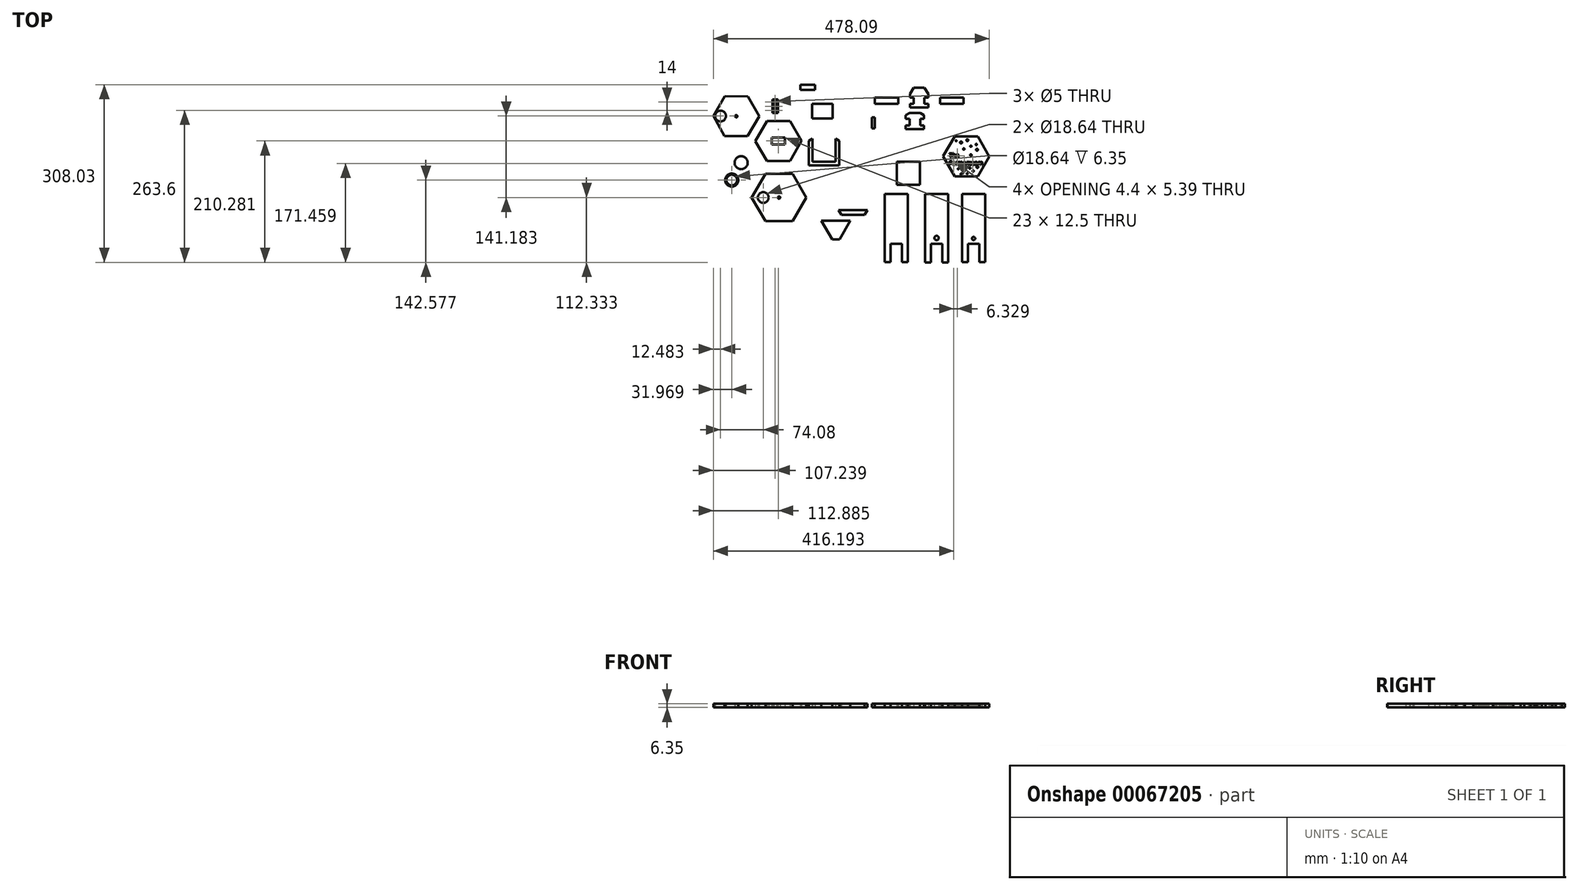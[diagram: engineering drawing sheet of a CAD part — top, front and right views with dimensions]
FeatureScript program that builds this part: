
annotation { "Feature Type Name" : "Feature", "Feature Type Description" : "" }
export const myFeature = defineFeature(function(context is Context, id is Id, definition is map)
    precondition{}
    {
        {
            var Q0;
            Q0=qCreatedBy(makeId("Top.planeOp"),FACE);
            var sketch = newSketch(context, id + "F0", { "sketchPlane" : qUnion([Q0])});
            skLineSegment(sketch, "E0.bottom", {"start": v(13.19, 75.62) * mm, "end": v(53.19, 75.62) * mm});
            skLineSegment(sketch, "E0.left", {"start": v(13.19, 75.62) * mm, "end": v(13.19, -42.73) * mm});
            skLineSegment(sketch, "E0.right", {"start": v(53.19, 75.62) * mm, "end": v(53.19, -42.73) * mm});
            skLineSegment(sketch, "E1.top", {"start": v(23.19, -10.73) * mm, "end": v(43.19, -10.73) * mm});
            skLineSegment(sketch, "E1.left", {"start": v(23.19, -42.73) * mm, "end": v(23.19, -10.73) * mm});
            skLineSegment(sketch, "E1.right", {"start": v(43.19, -42.73) * mm, "end": v(43.19, -10.73) * mm});
            skLineSegment(sketch, "E2", {"start": v(23.19, -42.73) * mm, "end": v(13.19, -42.73) * mm});
            skLineSegment(sketch, "E3", {"start": v(53.19, -42.73) * mm, "end": v(43.19, -42.73) * mm});
            skCircle(sketch, "E4.cCircle", {"center": v(-113.78, 34.64) * mm, "radius": 40 * mm, "construction": true});
            skLineSegment(sketch, "E4.0", {"start": v(-73.79, 34.86) * mm, "end": v(-93.6, 0.11) * mm});
            skLineSegment(sketch, "E4.1", {"start": v(-93.6, 0.11) * mm, "end": v(-133.6, -0.1) * mm});
            skLineSegment(sketch, "E4.2", {"start": v(-133.6, -0.1) * mm, "end": v(-153.78, 34.42) * mm});
            skLineSegment(sketch, "E4.3", {"start": v(-153.78, 34.42) * mm, "end": v(-133.97, 69.17) * mm});
            skLineSegment(sketch, "E4.4", {"start": v(-133.97, 69.17) * mm, "end": v(-93.98, 69.4) * mm});
            skLineSegment(sketch, "E4.5", {"start": v(-93.98, 69.4) * mm, "end": v(-73.79, 34.86) * mm});
            skCircle(sketch, "E5.cCircle", {"center": v(-112.79, -63.3) * mm, "radius": 47.33 * mm, "construction": true});
            skLineSegment(sketch, "E5.0", {"start": v(-89.12, -104.3) * mm, "end": v(-136.45, -104.3) * mm});
            skLineSegment(sketch, "E5.1", {"start": v(-136.45, -104.3) * mm, "end": v(-160.12, -63.3) * mm});
            skLineSegment(sketch, "E5.2", {"start": v(-160.12, -63.3) * mm, "end": v(-136.45, -22.32) * mm});
            skLineSegment(sketch, "E5.3", {"start": v(-136.45, -22.32) * mm, "end": v(-89.12, -22.32) * mm});
            skLineSegment(sketch, "E5.4", {"start": v(-89.12, -22.32) * mm, "end": v(-65.46, -63.3) * mm});
            skLineSegment(sketch, "E5.5", {"start": v(-65.46, -63.3) * mm, "end": v(-89.12, -104.3) * mm});
            skCircle(sketch, "E6", {"center": v(-112.79, -63.3) * mm, "radius": 2 * mm});
            skLineSegment(sketch, "E7", {"start": v(-112.79, -63.3) * mm, "end": v(-160.12, -63.3) * mm});
            skCircle(sketch, "E8", {"center": v(-140.1, -63.3) * mm, "radius": 9.32 * mm});
            skLineSegment(sketch, "E9", {"start": v(-130.79, -63.3) * mm, "end": v(-114.79, -63.3) * mm});
            skCircle(sketch, "E10", {"center": v(-178.44, -3) * mm, "radius": 11.32 * mm});
            skCircle(sketch, "E11.cCircle", {"center": v(211.42, 8.02) * mm, "radius": 40 * mm, "construction": true});
            skLineSegment(sketch, "E11.0", {"start": v(231.66, 42.52) * mm, "end": v(251.42, 7.74) * mm});
            skLineSegment(sketch, "E11.1", {"start": v(251.42, 7.74) * mm, "end": v(231.17, -26.76) * mm});
            skLineSegment(sketch, "E11.2", {"start": v(231.17, -26.76) * mm, "end": v(191.17, -26.48) * mm});
            skLineSegment(sketch, "E11.3", {"start": v(191.17, -26.48) * mm, "end": v(171.42, 8.3) * mm});
            skLineSegment(sketch, "E11.4", {"start": v(171.42, 8.3) * mm, "end": v(191.66, 42.8) * mm});
            skLineSegment(sketch, "E11.5", {"start": v(191.66, 42.8) * mm, "end": v(231.66, 42.52) * mm});
            skText(sketch, "E12", { "text": "The \nFermenteam", "fontName": "OpenSans-Regular.ttf"});
            skLineSegment(sketch, "E13.0", {"start": v(-8.24, -136.08) * mm, "end": v(-20.94, -136.08) * mm});
            skLineSegment(sketch, "E14", {"start": v(-39.59, -103.77) * mm, "end": v(10.41, -103.77) * mm});
            skLineSegment(sketch, "E15", {"start": v(-20.94, -136.08) * mm, "end": v(-39.59, -103.77) * mm});
            skLineSegment(sketch, "E16", {"start": v(-8.24, -136.08) * mm, "end": v(10.41, -103.77) * mm});
            skLineSegment(sketch, "E17", {"start": v(-9.58, -84.74) * mm, "end": v(40.42, -84.74) * mm});
            skLineSegment(sketch, "E18.0", {"start": v(35.42, -93.4) * mm, "end": v(-4.58, -93.4) * mm});
            skLineSegment(sketch, "E19", {"start": v(35.42, -93.4) * mm, "end": v(40.42, -84.74) * mm});
            skLineSegment(sketch, "E20", {"start": v(-4.58, -93.4) * mm, "end": v(-9.58, -84.74) * mm});
            skCircle(sketch, "E21", {"center": v(193.92, 34.98) * mm, "radius": 0.93 * mm});
            skCircle(sketch, "E22", {"center": v(202.28, 32.08) * mm, "radius": 1.74 * mm});
            skCircle(sketch, "E23.cCircle", {"center": v(-186.87, 77.62) * mm, "radius": 39.8 * mm, "construction": true});
            skLineSegment(sketch, "E23.0", {"start": v(-167.3, 42.96) * mm, "end": v(-207.1, 43.34) * mm});
            skLineSegment(sketch, "E23.1", {"start": v(-207.1, 43.34) * mm, "end": v(-226.67, 78) * mm});
            skLineSegment(sketch, "E23.2", {"start": v(-226.67, 78) * mm, "end": v(-206.44, 112.27) * mm});
            skLineSegment(sketch, "E23.3", {"start": v(-206.44, 112.27) * mm, "end": v(-166.64, 111.9) * mm});
            skLineSegment(sketch, "E23.4", {"start": v(-166.64, 111.9) * mm, "end": v(-147.07, 77.24) * mm});
            skLineSegment(sketch, "E23.5", {"start": v(-147.07, 77.24) * mm, "end": v(-167.3, 42.96) * mm});
            skCircle(sketch, "E24", {"center": v(213.2, 36.14) * mm, "radius": 1.66 * mm});
            skCircle(sketch, "E25", {"center": v(219.36, 25.57) * mm, "radius": 1.1 * mm});
            skCircle(sketch, "E26", {"center": v(207.04, 20.7) * mm, "radius": 1.3 * mm});
            skCircle(sketch, "E27", {"center": v(228.65, 28.6) * mm, "radius": 1.16 * mm});
            skCircle(sketch, "E28", {"center": v(230.04, 19.53) * mm, "radius": 1.66 * mm});
            skCircle(sketch, "E29", {"center": v(208.32, -15.2) * mm, "radius": 0.84 * mm});
            skCircle(sketch, "E30", {"center": v(223.38, -17.38) * mm, "radius": 1.2 * mm});
            skCircle(sketch, "E31", {"center": v(217.7, -12.44) * mm, "radius": 1.12 * mm});
            skCircle(sketch, "E32", {"center": v(197.6, -13.49) * mm, "radius": 0.82 * mm});
            skCircle(sketch, "E33", {"center": v(202.55, -22.64) * mm, "radius": 1.14 * mm});
            skCircle(sketch, "E34", {"center": v(212.88, -22.01) * mm, "radius": 0.77 * mm});
            skCircle(sketch, "E35", {"center": v(230.65, -10.5) * mm, "radius": 1.52 * mm});
            skCircle(sketch, "E36", {"center": v(219.28, 10.3) * mm, "radius": 1.41 * mm});
            skLineSegment(sketch, "E37.bottom", {"start": v(120.35, 127.23) * mm, "end": v(138.82, 127.23) * mm});
            skLineSegment(sketch, "E37.top", {"start": v(111.39, 92.46) * mm, "end": v(147.78, 92.46) * mm});
            skLineSegment(sketch, "E38", {"start": v(129.58, 92.46) * mm, "end": v(129.58, 110.79) * mm, "construction": true});
            skLineSegment(sketch, "E39.bottom", {"start": v(145.42, 92.46) * mm, "end": v(147.78, 92.46) * mm});
            skLineSegment(sketch, "E39.top", {"start": v(138.82, 98.81) * mm, "end": v(145.42, 98.81) * mm});
            skLineSegment(sketch, "E39.right", {"start": v(145.42, 92.46) * mm, "end": v(145.42, 98.81) * mm});
            skLineSegment(sketch, "E40.bottom", {"start": v(165.76, 98.81) * mm, "end": v(206.4, 98.81) * mm});
            skLineSegment(sketch, "E40.top", {"start": v(165.76, 109.97) * mm, "end": v(206.4, 109.97) * mm});
            skLineSegment(sketch, "E40.left", {"start": v(165.76, 98.81) * mm, "end": v(165.76, 109.97) * mm});
            skLineSegment(sketch, "E40.right", {"start": v(206.4, 98.81) * mm, "end": v(206.4, 109.97) * mm});
            skLineSegment(sketch, "E41.top", {"start": v(138.82, 109.97) * mm, "end": v(145.42, 109.97) * mm});
            skLineSegment(sketch, "E41.right", {"start": v(145.42, 116.46) * mm, "end": v(145.42, 109.97) * mm});
            skLineSegment(sketch, "E42", {"start": v(145.42, 116.46) * mm, "end": v(138.82, 127.23) * mm});
            skLineSegment(sketch, "E43", {"start": v(138.82, 109.97) * mm, "end": v(138.82, 98.81) * mm});
            skLineSegment(sketch, "E44", {"start": v(145.42, 109.97) * mm, "end": v(165.76, 109.97) * mm, "construction": true});
            skLineSegment(sketch, "E45", {"start": v(145.42, 98.81) * mm, "end": v(165.76, 98.81) * mm, "construction": true});
            skLineSegment(sketch, "E46", {"start": v(138.82, 127.23) * mm, "end": v(138.82, 109.97) * mm, "construction": true});
            skLineSegment(sketch, "E47.MirrorCS", {"start": v(93.4, 98.81) * mm, "end": v(93.4, 109.97) * mm});
            skLineSegment(sketch, "E48.MirrorCS", {"start": v(113.75, 109.97) * mm, "end": v(93.4, 109.97) * mm, "construction": true});
            skLineSegment(sketch, "E49.MirrorCS", {"start": v(93.4, 109.97) * mm, "end": v(52.77, 109.97) * mm});
            skLineSegment(sketch, "E50.MirrorCS", {"start": v(120.35, 109.97) * mm, "end": v(120.35, 98.81) * mm});
            skLineSegment(sketch, "E51.MirrorCS", {"start": v(93.4, 98.81) * mm, "end": v(52.77, 98.81) * mm});
            skLineSegment(sketch, "E52.MirrorCS", {"start": v(113.75, 116.46) * mm, "end": v(120.35, 127.23) * mm});
            skLineSegment(sketch, "E53.MirrorCS", {"start": v(113.75, 92.46) * mm, "end": v(113.75, 98.81) * mm});
            skLineSegment(sketch, "E54.MirrorCS", {"start": v(113.75, 116.46) * mm, "end": v(113.75, 109.97) * mm});
            skLineSegment(sketch, "E55.MirrorCS", {"start": v(120.35, 98.81) * mm, "end": v(113.75, 98.81) * mm});
            skLineSegment(sketch, "E56.MirrorCS", {"start": v(120.35, 109.97) * mm, "end": v(113.75, 109.97) * mm});
            skLineSegment(sketch, "E57.MirrorCS", {"start": v(113.75, 92.46) * mm, "end": v(111.39, 92.46) * mm});
            skLineSegment(sketch, "E58.MirrorCS", {"start": v(120.35, 127.23) * mm, "end": v(120.35, 109.97) * mm, "construction": true});
            skLineSegment(sketch, "E59.MirrorCS", {"start": v(52.77, 98.81) * mm, "end": v(52.77, 109.97) * mm});
            skLineSegment(sketch, "E60.MirrorCS", {"start": v(113.75, 98.81) * mm, "end": v(93.4, 98.81) * mm, "construction": true});
            skCircle(sketch, "E61", {"center": v(-194.7, -33.06) * mm, "radius": 11.32 * mm});
            skCircle(sketch, "E62", {"center": v(-194.7, -33.06) * mm, "radius": 9.32 * mm});
            skCircle(sketch, "E63", {"center": v(-194.7, -33.06) * mm, "radius": 12.32 * mm});
            skCircle(sketch, "E64", {"center": v(-186.87, 77.62) * mm, "radius": 2 * mm});
            skLineSegment(sketch, "E65", {"start": v(-226.67, 78) * mm, "end": v(-186.87, 77.62) * mm});
            skCircle(sketch, "E66", {"center": v(-214.19, 77.88) * mm, "radius": 9.32 * mm});
            skLineSegment(sketch, "E67", {"start": v(-188.87, 77.63) * mm, "end": v(-204.87, 77.79) * mm});
            skPoint(sketch, "E68.centerSnap0", {"position": v(33.19, 75.62) * mm});
            skLineSegment(sketch, "E69.bottom", {"start": v(113.25, 83.45) * mm, "end": v(131.72, 83.45) * mm});
            skLineSegment(sketch, "E70", {"start": v(131.72, 83.45) * mm, "end": v(131.72, 72.77) * mm, "construction": true});
            skLineSegment(sketch, "E71.top", {"start": v(131.72, 72.77) * mm, "end": v(138.32, 72.77) * mm});
            skLineSegment(sketch, "E72.MirrorCS", {"start": v(113.25, 72.77) * mm, "end": v(106.65, 72.77) * mm});
            skLineSegment(sketch, "E69.top", {"start": v(116.48, 55.26) * mm, "end": v(128.49, 55.26) * mm});
            skLineSegment(sketch, "E73.MirrorCS", {"start": v(113.25, 72.77) * mm, "end": v(113.25, 61.61) * mm});
            skLineSegment(sketch, "E74.top", {"start": v(131.72, 61.61) * mm, "end": v(138.32, 61.61) * mm});
            skLineSegment(sketch, "E75", {"start": v(122.48, 55.26) * mm, "end": v(122.48, 72.64) * mm, "construction": true});
            skLineSegment(sketch, "E76.MirrorCS", {"start": v(106.65, 72.77) * mm, "end": v(74.12, 72.77) * mm, "construction": true});
            skLineSegment(sketch, "E77.MirrorCS", {"start": v(116.48, 55.26) * mm, "end": v(106.65, 55.26) * mm});
            skLineSegment(sketch, "E71.right", {"start": v(138.32, 79.26) * mm, "end": v(138.32, 72.77) * mm});
            skLineSegment(sketch, "E78.MirrorCS", {"start": v(113.25, 83.45) * mm, "end": v(113.25, 72.77) * mm, "construction": true});
            skLineSegment(sketch, "E74.right", {"start": v(138.32, 55.26) * mm, "end": v(138.32, 61.61) * mm});
            skLineSegment(sketch, "E79", {"start": v(138.32, 79.26) * mm, "end": v(131.72, 83.45) * mm});
            skLineSegment(sketch, "E80.MirrorCS", {"start": v(106.65, 79.26) * mm, "end": v(113.25, 83.45) * mm});
            skLineSegment(sketch, "E81", {"start": v(131.72, 72.77) * mm, "end": v(131.72, 61.61) * mm});
            skLineSegment(sketch, "E74.bottom", {"start": v(128.49, 55.26) * mm, "end": v(138.32, 55.26) * mm});
            skLineSegment(sketch, "E82.MirrorCS", {"start": v(106.65, 55.26) * mm, "end": v(106.65, 61.61) * mm});
            skLineSegment(sketch, "E83", {"start": v(138.32, 72.77) * mm, "end": v(170.85, 72.77) * mm, "construction": true});
            skLineSegment(sketch, "E84.MirrorCS", {"start": v(106.65, 61.61) * mm, "end": v(86.31, 61.61) * mm, "construction": true});
            skLineSegment(sketch, "E85.MirrorCS", {"start": v(106.65, 79.26) * mm, "end": v(106.65, 72.77) * mm});
            skLineSegment(sketch, "E86", {"start": v(138.32, 61.61) * mm, "end": v(158.66, 61.61) * mm, "construction": true});
            skLineSegment(sketch, "E87.MirrorCS", {"start": v(113.25, 61.61) * mm, "end": v(106.65, 61.61) * mm});
            skLineSegment(sketch, "E88.rect.bottom", {"start": v(-102.28, 28.4) * mm, "end": v(-125.28, 28.4) * mm});
            skLineSegment(sketch, "E88.rect.top", {"start": v(-102.28, 40.9) * mm, "end": v(-125.28, 40.9) * mm});
            skLineSegment(sketch, "E88.rect.left", {"start": v(-102.28, 28.4) * mm, "end": v(-102.28, 40.9) * mm});
            skLineSegment(sketch, "E88.rect.right", {"start": v(-125.28, 28.4) * mm, "end": v(-125.28, 40.9) * mm});
            skLineSegment(sketch, "E89.bottom", {"start": v(-123.93, 106.46) * mm, "end": v(-114.93, 106.46) * mm});
            skLineSegment(sketch, "E89.top", {"start": v(-123.93, 83.46) * mm, "end": v(-114.93, 83.46) * mm});
            skLineSegment(sketch, "E89.left", {"start": v(-123.93, 106.46) * mm, "end": v(-123.93, 83.46) * mm});
            skLineSegment(sketch, "E89.right", {"start": v(-114.93, 106.46) * mm, "end": v(-114.93, 83.46) * mm});
            skLineSegment(sketch, "E90", {"start": v(-119.43, 106.46) * mm, "end": v(-119.43, 83.46) * mm});
            skCircle(sketch, "E91", {"center": v(-119.43, 101.96) * mm, "radius": 2.5 * mm});
            skCircle(sketch, "E92", {"center": v(-119.43, 94.96) * mm, "radius": 2.5 * mm});
            skCircle(sketch, "E93", {"center": v(-119.43, 87.96) * mm, "radius": 2.5 * mm});
            skLineSegment(sketch, "E94.bottom", {"start": v(131.41, -41.3) * mm, "end": v(91.41, -41.3) * mm});
            skLineSegment(sketch, "E94.top", {"start": v(131.41, -1.3) * mm, "end": v(91.41, -1.3) * mm});
            skLineSegment(sketch, "E94.left", {"start": v(131.41, -41.3) * mm, "end": v(131.41, -1.3) * mm});
            skLineSegment(sketch, "E94.right", {"start": v(91.41, -41.3) * mm, "end": v(91.41, -1.3) * mm});
            skPoint(sketch, "E94.middle", {"position": v(111.41, -21.3) * mm});
            skLineSegment(sketch, "E95.bottom", {"start": v(-50.7, 123.39) * mm, "end": v(-75.9, 123.39) * mm});
            skLineSegment(sketch, "E95.top", {"start": v(-50.7, 132.39) * mm, "end": v(-75.9, 132.39) * mm});
            skLineSegment(sketch, "E95.left", {"start": v(-50.7, 123.39) * mm, "end": v(-50.7, 132.39) * mm});
            skLineSegment(sketch, "E95.right", {"start": v(-75.9, 123.39) * mm, "end": v(-75.9, 132.39) * mm});
            skPoint(sketch, "E95.middle", {"position": v(-63.3, 127.89) * mm});
            skLineSegment(sketch, "E96.bottom", {"start": v(70.1, -56.84) * mm, "end": v(110.1, -56.84) * mm});
            skLineSegment(sketch, "E96.left", {"start": v(70.1, -56.84) * mm, "end": v(70.1, -175.19) * mm});
            skLineSegment(sketch, "E96.right", {"start": v(110.1, -56.84) * mm, "end": v(110.1, -175.19) * mm});
            skLineSegment(sketch, "E97.top", {"start": v(80.1, -143.19) * mm, "end": v(100.1, -143.19) * mm});
            skLineSegment(sketch, "E97.left", {"start": v(80.1, -175.19) * mm, "end": v(80.1, -143.19) * mm});
            skLineSegment(sketch, "E97.right", {"start": v(100.1, -175.19) * mm, "end": v(100.1, -143.19) * mm});
            skLineSegment(sketch, "E98", {"start": v(80.1, -175.19) * mm, "end": v(70.1, -175.19) * mm});
            skLineSegment(sketch, "E99", {"start": v(110.1, -175.19) * mm, "end": v(100.1, -175.19) * mm});
            skPoint(sketch, "E100.centerSnap0", {"position": v(90.1, -56.84) * mm});
            skLineSegment(sketch, "E101.bottom", {"start": v(139.95, -57.3) * mm, "end": v(179.95, -57.3) * mm});
            skLineSegment(sketch, "E101.left", {"start": v(139.95, -57.3) * mm, "end": v(139.95, -175.64) * mm});
            skLineSegment(sketch, "E101.right", {"start": v(179.95, -57.3) * mm, "end": v(179.95, -175.64) * mm});
            skLineSegment(sketch, "E102.top", {"start": v(149.95, -143.64) * mm, "end": v(169.95, -143.64) * mm});
            skLineSegment(sketch, "E102.left", {"start": v(149.95, -175.64) * mm, "end": v(149.95, -143.64) * mm});
            skLineSegment(sketch, "E102.right", {"start": v(169.95, -175.64) * mm, "end": v(169.95, -143.64) * mm});
            skLineSegment(sketch, "E103", {"start": v(149.95, -175.64) * mm, "end": v(139.95, -175.64) * mm});
            skLineSegment(sketch, "E104", {"start": v(179.95, -175.64) * mm, "end": v(169.95, -175.64) * mm});
            skPoint(sketch, "E105.centerSnap0", {"position": v(159.95, -57.3) * mm});
            skLineSegment(sketch, "E106", {"start": v(33.19, 75.62) * mm, "end": v(33.19, -10.73) * mm});
            skLineSegment(sketch, "E107", {"start": v(90.1, -56.84) * mm, "end": v(90.1, -143.19) * mm});
            skLineSegment(sketch, "E108", {"start": v(159.95, -57.3) * mm, "end": v(159.95, -143.64) * mm});
            skCircle(sketch, "E109", {"center": v(159.95, -133.48) * mm, "radius": 3.82 * mm});
            skLineSegment(sketch, "E110.bottom", {"start": v(-8.5, -7.82) * mm, "end": v(-61.2, -7.82) * mm});
            skLineSegment(sketch, "E110.top", {"start": v(-8.5, 44.88) * mm, "end": v(-61.2, 44.88) * mm});
            skLineSegment(sketch, "E110.left", {"start": v(-8.5, -7.82) * mm, "end": v(-8.5, 44.88) * mm});
            skLineSegment(sketch, "E110.right", {"start": v(-61.2, -7.82) * mm, "end": v(-61.2, 44.88) * mm});
            skPoint(sketch, "E110.middle", {"position": v(-34.84, 18.53) * mm});
            skLineSegment(sketch, "E111.bottom", {"start": v(-14.84, -1.47) * mm, "end": v(-54.84, -1.47) * mm});
            skLineSegment(sketch, "E111.top", {"start": v(-14.84, 38.53) * mm, "end": v(-54.84, 38.53) * mm});
            skLineSegment(sketch, "E111.left", {"start": v(-14.84, -1.47) * mm, "end": v(-14.84, 38.53) * mm});
            skLineSegment(sketch, "E111.right", {"start": v(-54.84, -1.47) * mm, "end": v(-54.84, 38.53) * mm});
            skLineSegment(sketch, "E112", {"start": v(-14.84, 38.53) * mm, "end": v(-8.5, 34.86) * mm});
            skLineSegment(sketch, "E113", {"start": v(-54.84, 38.53) * mm, "end": v(-61.2, 34.86) * mm});
            skLineSegment(sketch, "E114.bottom", {"start": v(204.1, -57.03) * mm, "end": v(244.1, -57.02) * mm});
            skLineSegment(sketch, "E114.left", {"start": v(204.1, -57.03) * mm, "end": v(204.1, -175.37) * mm});
            skLineSegment(sketch, "E114.right", {"start": v(244.1, -57.02) * mm, "end": v(244.1, -175.37) * mm});
            skLineSegment(sketch, "E115.top", {"start": v(214.1, -143.37) * mm, "end": v(234.1, -143.37) * mm});
            skLineSegment(sketch, "E115.left", {"start": v(214.1, -175.37) * mm, "end": v(214.1, -143.37) * mm});
            skLineSegment(sketch, "E115.right", {"start": v(234.1, -175.37) * mm, "end": v(234.1, -143.37) * mm});
            skLineSegment(sketch, "E116", {"start": v(214.1, -175.37) * mm, "end": v(204.1, -175.37) * mm});
            skLineSegment(sketch, "E117", {"start": v(244.1, -175.37) * mm, "end": v(234.1, -175.37) * mm});
            skPoint(sketch, "E118.centerSnap0", {"position": v(224.1, -57.03) * mm});
            skLineSegment(sketch, "E119", {"start": v(224.1, -57.03) * mm, "end": v(224.1, -143.37) * mm});
            skCircle(sketch, "E120", {"center": v(224.1, -134.27) * mm, "radius": 2.75 * mm});
            skLineSegment(sketch, "E121.bottom", {"start": v(116.41, 5.76) * mm, "end": v(106.41, 5.76) * mm});
            skLineSegment(sketch, "E121.top", {"start": v(116.41, -48.34) * mm, "end": v(106.41, -48.34) * mm});
            skLineSegment(sketch, "E121.left", {"start": v(116.41, 5.76) * mm, "end": v(116.41, -48.34) * mm});
            skLineSegment(sketch, "E121.right", {"start": v(106.41, 5.76) * mm, "end": v(106.41, -48.34) * mm});
            skLineSegment(sketch, "E122.bottom", {"start": v(-55.47, 98.98) * mm, "end": v(-19.77, 98.98) * mm});
            skLineSegment(sketch, "E122.top", {"start": v(-55.47, 73.78) * mm, "end": v(-19.77, 73.78) * mm});
            skLineSegment(sketch, "E122.left", {"start": v(-55.47, 98.98) * mm, "end": v(-55.47, 73.78) * mm});
            skLineSegment(sketch, "E122.right", {"start": v(-19.77, 98.98) * mm, "end": v(-19.77, 73.78) * mm});
            skLineSegment(sketch, "E123.bottom", {"start": v(53.19, 75.62) * mm, "end": v(48.19, 75.62) * mm});
            skLineSegment(sketch, "E123.top", {"start": v(53.19, 56.27) * mm, "end": v(48.19, 56.27) * mm});
            skLineSegment(sketch, "E123.left", {"start": v(53.19, 75.62) * mm, "end": v(53.19, 56.27) * mm});
            skLineSegment(sketch, "E123.right", {"start": v(48.19, 75.62) * mm, "end": v(48.19, 56.27) * mm});
            skLineSegment(sketch, "E124", {"start": v(48.19, 64.27) * mm, "end": v(53.19, 64.27) * mm});
            skCircle(sketch, "E125", {"center": v(33.19, 5.62) * mm, "radius": 2.6 * mm});
            const initialGuessF0  = {"E12": [0.18176, 0.00644, 1, 0, 0.007]};
            skSetInitialGuess(sketch, initialGuessF0);
            skSolve(sketch);
        }
        {
            var Q0;
            Q0=makeQuery(id+"F0.imprint","IMPRINT",FACE,{"disambiguationData":[TD([[makeQuery(id+"F0.imprint","IMPRINT",EDGE,{"derivedFrom":sQuery(id+"F0.wireOp",EDGE,"E4.0")}),-1.0]])]});
            var Q1;
            Q1=makeQuery(id+"F0.imprint","IMPRINT",FACE,{"disambiguationData":[TD([[makeQuery(id+"F0.imprint","IMPRINT",EDGE,{"derivedFrom":sQuery(id+"F0.wireOp",EDGE,"E10")}),1.0]])]});
            var Q2;
            Q2=makeQuery(id+"F0.imprint","IMPRINT",FACE,{"disambiguationData":[TD([[makeQuery(id+"F0.imprint","IMPRINT",EDGE,{"derivedFrom":sQuery(id+"F0.wireOp",EDGE,"E13.0")}),-1.0]])]});
            var Q3;
            Q3=makeQuery(id+"F0.imprint","IMPRINT",FACE,{"disambiguationData":[TD([[makeQuery(id+"F0.imprint","IMPRINT",EDGE,{"derivedFrom":sQuery(id+"F0.wireOp",EDGE,"E17")}),-1.0]])]});
            var Q4;
            Q4=makeQuery(id+"F0.imprint","IMPRINT",FACE,{"disambiguationData":[TD([[makeQuery(id+"F0.imprint","IMPRINT",EDGE,{"derivedFrom":sQuery(id+"F0.wireOp",EDGE,"E37.bottom")}),-1.0]])]});
            var Q5;
            Q5=makeQuery(id+"F0.imprint","IMPRINT",FACE,{"disambiguationData":[TD([[makeQuery(id+"F0.imprint","IMPRINT",EDGE,{"derivedFrom":sQuery(id+"F0.wireOp",EDGE,"E40.bottom")}),1.0]])]});
            var Q6;
            Q6=makeQuery(id+"F0.imprint","IMPRINT",FACE,{"disambiguationData":[TD([[makeQuery(id+"F0.imprint","IMPRINT",EDGE,{"derivedFrom":sQuery(id+"F0.wireOp",EDGE,"E47.MirrorCS")}),1.0]])]});
            var Q7;
            Q7=makeQuery(id+"F0.imprint","IMPRINT",FACE,{"disambiguationData":[TD([[makeQuery(id+"F0.imprint","IMPRINT",EDGE,{"derivedFrom":sQuery(id+"F0.wireOp",EDGE,"E0.bottom")}),-1.0]])]});
            var Q8;
            Q8=makeQuery(id+"F0.imprint","IMPRINT",FACE,{"disambiguationData":[TD([[makeQuery(id+"F0.imprint","IMPRINT",EDGE,{"derivedFrom":sQuery(id+"F0.wireOp",EDGE,"E61")}),1.0]])]});
            var Q9;
            Q9=makeQuery(id+"F0.imprint","IMPRINT",FACE,{"disambiguationData":[TD([[makeQuery(id+"F0.imprint","IMPRINT",EDGE,{"derivedFrom":sQuery(id+"F0.wireOp",EDGE,"E5.0")}),-1.0]])]});
            var Q10;
            Q10=makeQuery(id+"F0.imprint","IMPRINT",FACE,{"disambiguationData":[TD([[makeQuery(id+"F0.imprint","IMPRINT",EDGE,{"derivedFrom":sQuery(id+"F0.wireOp",EDGE,"E23.0")}),-1.0]])]});
            var Q11;
            Q11=makeQuery(id+"F0.imprint","IMPRINT",FACE,{"disambiguationData":[TD([[makeQuery(id+"F0.imprint","IMPRINT",EDGE,{"derivedFrom":sQuery(id+"F0.wireOp",EDGE,"E4.0")}),-1.0]])]});
            var Q12;
            Q12=makeQuery(id+"F0.imprint","IMPRINT",FACE,{"disambiguationData":[TD([[makeQuery(id+"F0.imprint","IMPRINT",EDGE,{"derivedFrom":sQuery(id+"F0.wireOp",EDGE,"E10")}),1.0]])]});
            var Q13;
            Q13=makeQuery(id+"F0.imprint","IMPRINT",FACE,{"disambiguationData":[TD([[makeQuery(id+"F0.imprint","IMPRINT",EDGE,{"derivedFrom":sQuery(id+"F0.wireOp",EDGE,"E13.0")}),-1.0]])]});
            var Q14;
            Q14=makeQuery(id+"F0.imprint","IMPRINT",FACE,{"disambiguationData":[TD([[makeQuery(id+"F0.imprint","IMPRINT",EDGE,{"derivedFrom":sQuery(id+"F0.wireOp",EDGE,"E17")}),-1.0]])]});
            var Q15;
            Q15=makeQuery(id+"F0.imprint","IMPRINT",FACE,{"disambiguationData":[TD([[makeQuery(id+"F0.imprint","IMPRINT",EDGE,{"derivedFrom":sQuery(id+"F0.wireOp",EDGE,"E37.bottom")}),-1.0]])]});
            var Q16;
            Q16=makeQuery(id+"F0.imprint","IMPRINT",FACE,{"disambiguationData":[TD([[makeQuery(id+"F0.imprint","IMPRINT",EDGE,{"derivedFrom":sQuery(id+"F0.wireOp",EDGE,"E40.bottom")}),1.0]])]});
            var Q17;
            Q17=makeQuery(id+"F0.imprint","IMPRINT",FACE,{"disambiguationData":[TD([[makeQuery(id+"F0.imprint","IMPRINT",EDGE,{"derivedFrom":sQuery(id+"F0.wireOp",EDGE,"E47.MirrorCS")}),1.0]])]});
            var Q18;
            Q18=makeQuery(id+"F0.imprint","IMPRINT",FACE,{"disambiguationData":[TD([[makeQuery(id+"F0.imprint","IMPRINT",EDGE,{"derivedFrom":sQuery(id+"F0.wireOp",EDGE,"E0.bottom")}),-1.0]])]});
            var Q19;
            Q19=makeQuery(id+"F0.imprint","IMPRINT",FACE,{"disambiguationData":[TD([[makeQuery(id+"F0.imprint","IMPRINT",EDGE,{"derivedFrom":sQuery(id+"F0.wireOp",EDGE,"E61")}),1.0]])]});
            var Q20;
            Q20=makeQuery(id+"F0.imprint","IMPRINT",FACE,{"disambiguationData":[TD([[makeQuery(id+"F0.imprint","IMPRINT",EDGE,{"derivedFrom":sQuery(id+"F0.wireOp",EDGE,"E5.0")}),-1.0]])]});
            var Q21;
            Q21=makeQuery(id+"F0.imprint","IMPRINT",FACE,{"disambiguationData":[TD([[makeQuery(id+"F0.imprint","IMPRINT",EDGE,{"derivedFrom":sQuery(id+"F0.wireOp",EDGE,"E23.0")}),-1.0]])]});
            var Q22;
            Q22=makeQuery(id+"F0.imprint","IMPRINT",FACE,{"disambiguationData":[TD([[makeQuery(id+"F0.imprint","IMPRINT",EDGE,{"derivedFrom":sQuery(id+"F0.wireOp",EDGE,"E61")}),1.0]])]});
            var Q23;
            Q23=makeQuery(id+"F0.imprint","IMPRINT",FACE,{"disambiguationData":[TD([[makeQuery(id+"F0.imprint","IMPRINT",EDGE,{"derivedFrom":sQuery(id+"F0.wireOp",EDGE,"E11.0")}),-1.0]])]});
            var Q24;
            {var subQ5=sQuery(id+"F0.wireOp",EDGE,"E89.left");Q24=makeQuery(id+"F0.imprint","IMPRINT",FACE,{"disambiguationData":[TD([[makeQuery(id+"F0.imprint","IMPRINT",EDGE,{"derivedFrom":subQ5}),1.0]])]});}
            var Q25;
            {var subQ5=sQuery(id+"F0.wireOp",EDGE,"E89.right");Q25=makeQuery(id+"F0.imprint","IMPRINT",FACE,{"disambiguationData":[TD([[makeQuery(id+"F0.imprint","IMPRINT",EDGE,{"derivedFrom":subQ5}),-1.0]])]});}
            var Q26;
            Q26=makeQuery(id+"F0.imprint","IMPRINT",FACE,{"disambiguationData":[TD([[makeQuery(id+"F0.imprint","IMPRINT",EDGE,{"derivedFrom":sQuery(id+"F0.wireOp",EDGE,"E95.bottom")}),-1.0]])]});
            var Q27;
            {var subQ1=sQuery(id+"F0.wireOp",EDGE,"E110.bottom");Q27=makeQuery(id+"F0.imprint","IMPRINT",FACE,{"disambiguationData":[TD([[makeQuery(id+"F0.imprint","IMPRINT",EDGE,{"derivedFrom":subQ1}),-1.0]])]});}
            var Q28;
            Q28=makeQuery(id+"F0.imprint","IMPRINT",FACE,{"disambiguationData":[TD([[makeQuery(id+"F0.imprint","IMPRINT",EDGE,{"derivedFrom":sQuery(id+"F0.wireOp",EDGE,"E94.bottom")}),-1.0]])]});
            var Q29;
            {var subQ8=sQuery(id+"F0.wireOp",EDGE,"E96.right");Q29=makeQuery(id+"F0.imprint","IMPRINT",FACE,{"disambiguationData":[TD([[makeQuery(id+"F0.imprint","IMPRINT",EDGE,{"derivedFrom":subQ8}),-1.0]])]});}
            var Q30;
            {var subQ7=sQuery(id+"F0.wireOp",EDGE,"E96.left");Q30=makeQuery(id+"F0.imprint","IMPRINT",FACE,{"disambiguationData":[TD([[makeQuery(id+"F0.imprint","IMPRINT",EDGE,{"derivedFrom":subQ7}),1.0]])]});}
            var Q31;
            {var subQ4=sQuery(id+"F0.wireOp",EDGE,"E101.left");Q31=makeQuery(id+"F0.imprint","IMPRINT",FACE,{"disambiguationData":[TD([[makeQuery(id+"F0.imprint","IMPRINT",EDGE,{"derivedFrom":subQ4}),1.0]])]});}
            var Q32;
            {var subQ8=sQuery(id+"F0.wireOp",EDGE,"E101.right");Q32=makeQuery(id+"F0.imprint","IMPRINT",FACE,{"disambiguationData":[TD([[makeQuery(id+"F0.imprint","IMPRINT",EDGE,{"derivedFrom":subQ8}),-1.0]])]});}
            var Q33;
            {var subQ8=sQuery(id+"F0.wireOp",EDGE,"E114.left");Q33=makeQuery(id+"F0.imprint","IMPRINT",FACE,{"disambiguationData":[TD([[makeQuery(id+"F0.imprint","IMPRINT",EDGE,{"derivedFrom":subQ8}),1.0]])]});}
            var Q34;
            {var subQ3=sQuery(id+"F0.wireOp",EDGE,"50b46a36-ce94-46d7-8646-d56a16b42dbd.right");Q34=makeQuery(id+"F0.imprint","IMPRINT",FACE,{"disambiguationData":[TD([[makeQuery(id+"F0.imprint","IMPRINT",EDGE,{"derivedFrom":subQ3}),-1.0]])]});}
            var Q35;
            {var subQ3=sQuery(id+"F0.wireOp",EDGE,"50b46a36-ce94-46d7-8646-d56a16b42dbd.left");Q35=makeQuery(id+"F0.imprint","IMPRINT",FACE,{"disambiguationData":[TD([[makeQuery(id+"F0.imprint","IMPRINT",EDGE,{"derivedFrom":subQ3}),1.0]])]});}
            var Q36;
            {var subQ0=sQuery(id+"F0.wireOp",EDGE,"c86ab096-2162-46f3-b5a0-1120cb3be196.bottom");Q36=makeQuery(id+"F0.imprint","IMPRINT",FACE,{"disambiguationData":[TD([[makeQuery(id+"F0.imprint","IMPRINT",EDGE,{"derivedFrom":subQ0}),-1.0]])]});}
            var Q37;
            {var subQ3=sQuery(id+"F0.wireOp",EDGE,"74697473-444c-43b7-ace5-064c43f62069.bottom");Q37=makeQuery(id+"F0.imprint","IMPRINT",FACE,{"disambiguationData":[TD([[makeQuery(id+"F0.imprint","IMPRINT",EDGE,{"derivedFrom":subQ3}),-1.0]])]});}
            var Q38;
            Q38=makeQuery(id+"F0.imprint","IMPRINT",FACE,{"disambiguationData":[TD([[makeQuery(id+"F0.imprint","IMPRINT",EDGE,{"derivedFrom":sQuery(id+"F0.wireOp",EDGE,"E122.bottom")}),-1.0]])]});
            var Q39;
            {var subQ0=sQuery(id+"F0.wireOp",EDGE,"h4BFRYed-4b3C-ck0F-Lmz0-yU6Q0wIGrpGP");Q39=makeQuery(id+"F0.imprint","IMPRINT",FACE,{"disambiguationData":[TD([[makeQuery(id+"F0.imprint","IMPRINT",EDGE,{"derivedFrom":subQ0}),-1.0]])]});}
            var Q40;
            {var subQ4=sQuery(id+"F0.wireOp",EDGE,"dbddea4b-3583-442b-b685-0caf6d9bb7dc");Q40=makeQuery(id+"F0.imprint","IMPRINT",FACE,{"disambiguationData":[TD([[makeQuery(id+"F0.imprint","IMPRINT",EDGE,{"derivedFrom":subQ4}),1.0]])]});}
            var Q41;
            {var subQ4=sQuery(id+"F0.wireOp",EDGE,"7e951e3d-2b0a-43c5-b596-455d4c67541f");Q41=makeQuery(id+"F0.imprint","IMPRINT",FACE,{"disambiguationData":[TD([[makeQuery(id+"F0.imprint","IMPRINT",EDGE,{"derivedFrom":subQ4}),-1.0]])]});}
            var Q42;
            {var subQ0=sQuery(id+"F0.wireOp",EDGE,"p007L474-fs4W-K8oh-27Qv-Ib7xM6mkYaqR.bottom");var subQ1=sQuery(id+"F0.wireOp",EDGE,"c86ab096-2162-46f3-b5a0-1120cb3be196.left");var subQ2=makeQuery(id+"F0.imprint","INTERSECT",VERTEX,{"derivedFrom":[subQ1,subQ0]});Q42=makeQuery(id+"F0.imprint","IMPRINT",FACE,{"disambiguationData":[TD([[makeQuery(id+"F0.imprint","IMPRINT",EDGE,{"disambiguationData":[TD([[subQ2,-1.0]])],"derivedFrom":subQ1}),1.0]])]});}
            var Q43;
            {var subQ3=sQuery(id+"F0.wireOp",EDGE,"uQRnaVKu-mW2g-u7ST-Vl56-gffJsiD0h2sY");Q43=makeQuery(id+"F0.imprint","IMPRINT",FACE,{"disambiguationData":[TD([[makeQuery(id+"F0.imprint","IMPRINT",EDGE,{"derivedFrom":subQ3}),-1.0]])]});}
            var Q44;
            {var subQ0=sQuery(id+"F0.wireOp",EDGE,"swIfH0Nz-1cX9-DvDL-fieS-Ar0krU4vTFFK");Q44=makeQuery(id+"F0.imprint","IMPRINT",FACE,{"disambiguationData":[TD([[makeQuery(id+"F0.imprint","IMPRINT",EDGE,{"derivedFrom":subQ0}),-1.0]])]});}
            var Q45;
            {var subQ5=sQuery(id+"F0.wireOp",EDGE,"UeUgb8Ho-T7bt-SZKg-dOa7-EbF9aWgyKJtY");Q45=makeQuery(id+"F0.imprint","IMPRINT",FACE,{"disambiguationData":[TD([[makeQuery(id+"F0.imprint","IMPRINT",EDGE,{"derivedFrom":subQ5}),-1.0]])]});}
            var Q46;
            {var subQ5=sQuery(id+"F0.wireOp",EDGE,"Fs9yyLkr-EKqI-GmBq-qL5X-aLAriYqJqrEP");Q46=makeQuery(id+"F0.imprint","IMPRINT",FACE,{"disambiguationData":[TD([[makeQuery(id+"F0.imprint","IMPRINT",EDGE,{"derivedFrom":subQ5}),-1.0]])]});}
            var Q47;
            {var subQ6=sQuery(id+"F0.wireOp",EDGE,"mhGNEit0-hEs5-PI8g-1KAn-jS3QN26kYUXt");Q47=makeQuery(id+"F0.imprint","IMPRINT",FACE,{"disambiguationData":[TD([[makeQuery(id+"F0.imprint","IMPRINT",EDGE,{"derivedFrom":subQ6}),-1.0]])]});}
            var Q48;
            {var subQ0=sQuery(id+"F0.wireOp",EDGE,"96faf9ee-8a9b-491a-8ac7-1eba4b2c609e.top");Q48=makeQuery(id+"F0.imprint","IMPRINT",FACE,{"disambiguationData":[TD([[makeQuery(id+"F0.imprint","IMPRINT",EDGE,{"derivedFrom":subQ0}),-1.0]])]});}
            var Q49;
            {var subQ0=sQuery(id+"F0.wireOp",EDGE,"IzWmzehR-qbRP-L9kc-j4zw-mZ5IL3RcmAmy");Q49=makeQuery(id+"F0.imprint","IMPRINT",FACE,{"disambiguationData":[TD([[makeQuery(id+"F0.imprint","IMPRINT",EDGE,{"derivedFrom":subQ0}),1.0]])]});}
            var Q50;
            {var subQ5=sQuery(id+"F0.wireOp",EDGE,"8ezwI1NI-lKdW-U6zM-T5Ls-aygNhPswrC9t");Q50=makeQuery(id+"F0.imprint","IMPRINT",FACE,{"disambiguationData":[TD([[makeQuery(id+"F0.imprint","IMPRINT",EDGE,{"derivedFrom":subQ5}),1.0]])]});}
            var Q51;
            {var subQ0=sQuery(id+"F0.wireOp",EDGE,"QQY3Blda-cWIL-XZ22-1Vk1-Kx0ZYipli6Ji.top");var subQ1=sQuery(id+"F0.wireOp",EDGE,"BSUAY7Uk-Cua9-6rOF-vKWl-l1QNFl27aj1w");var subQ2=makeQuery(id+"F0.imprint","INTERSECT",VERTEX,{"derivedFrom":[subQ1,subQ0]});Q51=makeQuery(id+"F0.imprint","IMPRINT",FACE,{"disambiguationData":[TD([[makeQuery(id+"F0.imprint","IMPRINT",EDGE,{"disambiguationData":[TD([[subQ2,-1.0]])],"derivedFrom":subQ1}),1.0]])]});}
            var Q52;
            {var subQ0=sQuery(id+"F0.wireOp",EDGE,"3adfaaeb-48b6-467c-a537-47fc3dc6a6c0.left");Q52=makeQuery(id+"F0.imprint","IMPRINT",FACE,{"disambiguationData":[TD([[makeQuery(id+"F0.imprint","IMPRINT",EDGE,{"derivedFrom":subQ0}),1.0]])]});}
            var Q53;
            {var subQ0=sQuery(id+"F0.wireOp",EDGE,"860cfe5d-25c9-4f5e-8e16-f1d030cc68f1.left");var subQ1=sQuery(id+"F0.wireOp",EDGE,"3adfaaeb-48b6-467c-a537-47fc3dc6a6c0.bottom");var subQ2=makeQuery(id+"F0.imprint","INTERSECT",VERTEX,{"derivedFrom":[subQ1,subQ0]});Q53=makeQuery(id+"F0.imprint","IMPRINT",FACE,{"disambiguationData":[TD([[makeQuery(id+"F0.imprint","IMPRINT",EDGE,{"disambiguationData":[TD([[subQ2,-1.0]])],"derivedFrom":subQ1}),-1.0]])]});}
            var Q54;
            {var subQ0=sQuery(id+"F0.wireOp",EDGE,"3adfaaeb-48b6-467c-a537-47fc3dc6a6c0.right");Q54=makeQuery(id+"F0.imprint","IMPRINT",FACE,{"disambiguationData":[TD([[makeQuery(id+"F0.imprint","IMPRINT",EDGE,{"derivedFrom":subQ0}),-1.0]])]});}
            var Q55;
            {var subQ5=sQuery(id+"F0.wireOp",EDGE,"860cfe5d-25c9-4f5e-8e16-f1d030cc68f1.bottom");Q55=makeQuery(id+"F0.imprint","IMPRINT",FACE,{"disambiguationData":[TD([[makeQuery(id+"F0.imprint","IMPRINT",EDGE,{"derivedFrom":subQ5}),1.0]])]});}
            var Q56;
            {var subQ5=sQuery(id+"F0.wireOp",EDGE,"860cfe5d-25c9-4f5e-8e16-f1d030cc68f1.top");Q56=makeQuery(id+"F0.imprint","IMPRINT",FACE,{"disambiguationData":[TD([[makeQuery(id+"F0.imprint","IMPRINT",EDGE,{"derivedFrom":subQ5}),-1.0]])]});}
            var Q57;
            {var subQ0=sQuery(id+"F0.wireOp",EDGE,"2ec601c6-c0e0-4266-99cd-1b6f42becada.left");var subQ1=sQuery(id+"F0.wireOp",EDGE,"69915b46-6bfa-481c-96da-c66e9b5b28c9.bottom");var subQ2=makeQuery(id+"F0.imprint","INTERSECT",VERTEX,{"derivedFrom":[subQ1,subQ0]});Q57=makeQuery(id+"F0.imprint","IMPRINT",FACE,{"disambiguationData":[TD([[makeQuery(id+"F0.imprint","IMPRINT",EDGE,{"disambiguationData":[TD([[subQ2,-1.0]])],"derivedFrom":subQ1}),-1.0]])]});}
            var Q58;
            {var subQ0=sQuery(id+"F0.wireOp",EDGE,"69915b46-6bfa-481c-96da-c66e9b5b28c9.left");Q58=makeQuery(id+"F0.imprint","IMPRINT",FACE,{"disambiguationData":[TD([[makeQuery(id+"F0.imprint","IMPRINT",EDGE,{"derivedFrom":subQ0}),1.0]])]});}
            var Q59;
            {var subQ0=sQuery(id+"F0.wireOp",EDGE,"69915b46-6bfa-481c-96da-c66e9b5b28c9.right");Q59=makeQuery(id+"F0.imprint","IMPRINT",FACE,{"disambiguationData":[TD([[makeQuery(id+"F0.imprint","IMPRINT",EDGE,{"derivedFrom":subQ0}),-1.0]])]});}
            var Q60;
            {var subQ5=sQuery(id+"F0.wireOp",EDGE,"2ec601c6-c0e0-4266-99cd-1b6f42becada.bottom");Q60=makeQuery(id+"F0.imprint","IMPRINT",FACE,{"disambiguationData":[TD([[makeQuery(id+"F0.imprint","IMPRINT",EDGE,{"derivedFrom":subQ5}),1.0]])]});}
            var Q61;
            {var subQ5=sQuery(id+"F0.wireOp",EDGE,"2ec601c6-c0e0-4266-99cd-1b6f42becada.top");Q61=makeQuery(id+"F0.imprint","IMPRINT",FACE,{"disambiguationData":[TD([[makeQuery(id+"F0.imprint","IMPRINT",EDGE,{"derivedFrom":subQ5}),-1.0]])]});}
            var Q62;
            {var subQ0=sQuery(id+"F0.wireOp",EDGE,"T8THPtRh-4wBK-WFKN-r0CF-FVaLjCThY6Mf.bottom");var subQ1=sQuery(id+"F0.wireOp",EDGE,"8e509be8-d101-4c74-8c6d-f068b411a6e5.left");var subQ2=makeQuery(id+"F0.imprint","INTERSECT",VERTEX,{"derivedFrom":[subQ1,subQ0]});Q62=makeQuery(id+"F0.imprint","IMPRINT",FACE,{"disambiguationData":[TD([[makeQuery(id+"F0.imprint","IMPRINT",EDGE,{"disambiguationData":[TD([[subQ2,-1.0]])],"derivedFrom":subQ1}),-1.0]])]});}
            var Q63;
            {var subQ5=sQuery(id+"F0.wireOp",EDGE,"T8THPtRh-4wBK-WFKN-r0CF-FVaLjCThY6Mf.left");Q63=makeQuery(id+"F0.imprint","IMPRINT",FACE,{"disambiguationData":[TD([[makeQuery(id+"F0.imprint","IMPRINT",EDGE,{"derivedFrom":subQ5}),-1.0]])]});}
            var Q64;
            {var subQ5=sQuery(id+"F0.wireOp",EDGE,"T8THPtRh-4wBK-WFKN-r0CF-FVaLjCThY6Mf.right");Q64=makeQuery(id+"F0.imprint","IMPRINT",FACE,{"disambiguationData":[TD([[makeQuery(id+"F0.imprint","IMPRINT",EDGE,{"derivedFrom":subQ5}),1.0]])]});}
            var Q65;
            {var subQ0=sQuery(id+"F0.wireOp",EDGE,"8e509be8-d101-4c74-8c6d-f068b411a6e5.bottom");Q65=makeQuery(id+"F0.imprint","IMPRINT",FACE,{"disambiguationData":[TD([[makeQuery(id+"F0.imprint","IMPRINT",EDGE,{"derivedFrom":subQ0}),1.0]])]});}
            var Q66;
            {var subQ0=sQuery(id+"F0.wireOp",EDGE,"8e509be8-d101-4c74-8c6d-f068b411a6e5.top");Q66=makeQuery(id+"F0.imprint","IMPRINT",FACE,{"disambiguationData":[TD([[makeQuery(id+"F0.imprint","IMPRINT",EDGE,{"derivedFrom":subQ0}),-1.0]])]});}
            var Q67;
            {var subQ0=sQuery(id+"F0.wireOp",EDGE,"860cfe5d-25c9-4f5e-8e16-f1d030cc68f1.left");var subQ1=sQuery(id+"F0.wireOp",EDGE,"3adfaaeb-48b6-467c-a537-47fc3dc6a6c0.top");var subQ2=makeQuery(id+"F0.imprint","INTERSECT",VERTEX,{"derivedFrom":[subQ1,subQ0]});Q67=makeQuery(id+"F0.imprint","IMPRINT",FACE,{"disambiguationData":[TD([[makeQuery(id+"F0.imprint","IMPRINT",EDGE,{"disambiguationData":[TD([[subQ2,-1.0]])],"derivedFrom":subQ1}),1.0]])]});}
            var Q68;
            {var subQ0=sQuery(id+"F0.wireOp",EDGE,"799IjRvJ-Dktj-fwi9-RhBs-Kj844kSm7Izh");Q68=makeQuery(id+"F0.imprint","IMPRINT",FACE,{"disambiguationData":[TD([[makeQuery(id+"F0.imprint","IMPRINT",EDGE,{"derivedFrom":subQ0}),1.0]])]});}
            var Q69;
            {var subQ0=sQuery(id+"F0.wireOp",EDGE,"Aswungax-Nwtp-EKMZ-MuMH-U5RFGtTHexSd");Q69=makeQuery(id+"F0.imprint","IMPRINT",FACE,{"disambiguationData":[TD([[makeQuery(id+"F0.imprint","IMPRINT",EDGE,{"derivedFrom":subQ0}),1.0]])]});}
            var Q70;
            {var subQ5=sQuery(id+"F0.wireOp",EDGE,"YiqkaKLR-4Dmx-IN0i-HcmR-PsK4lVufwlE0.left");Q70=makeQuery(id+"F0.imprint","IMPRINT",FACE,{"disambiguationData":[TD([[makeQuery(id+"F0.imprint","IMPRINT",EDGE,{"derivedFrom":subQ5}),-1.0]])]});}
            var Q71;
            {var subQ0=sQuery(id+"F0.wireOp",EDGE,"642ae80b-53ca-425f-9e1c-665031984c0c.right");var subQ1=sQuery(id+"F0.wireOp",EDGE,"642ae80b-53ca-425f-9e1c-665031984c0c.top");var subQ2=makeQuery(id+"F0.imprint","INTERSECT",VERTEX,{"derivedFrom":[subQ1,subQ0]});Q71=makeQuery(id+"F0.imprint","IMPRINT",FACE,{"disambiguationData":[TD([[makeQuery(id+"F0.imprint","IMPRINT",EDGE,{"disambiguationData":[TD([[subQ2,1.0]])],"derivedFrom":subQ1}),1.0]])]});}
            var Q72;
            {var subQ0=sQuery(id+"F0.wireOp",EDGE,"419c5b55-3d34-4837-8a7f-80514d8a6413.left");var subQ1=sQuery(id+"F0.wireOp",EDGE,"642ae80b-53ca-425f-9e1c-665031984c0c.top");var subQ2=makeQuery(id+"F0.imprint","INTERSECT",VERTEX,{"derivedFrom":[subQ1,subQ0]});Q72=makeQuery(id+"F0.imprint","IMPRINT",FACE,{"disambiguationData":[TD([[makeQuery(id+"F0.imprint","IMPRINT",EDGE,{"disambiguationData":[TD([[subQ2,-1.0]])],"derivedFrom":subQ1}),1.0]])]});}
            var Q73;
            {var subQ0=sQuery(id+"F0.wireOp",EDGE,"642ae80b-53ca-425f-9e1c-665031984c0c.left");var subQ1=sQuery(id+"F0.wireOp",EDGE,"642ae80b-53ca-425f-9e1c-665031984c0c.top");var subQ2=makeQuery(id+"F0.imprint","INTERSECT",VERTEX,{"derivedFrom":[subQ1,subQ0]});Q73=makeQuery(id+"F0.imprint","IMPRINT",FACE,{"disambiguationData":[TD([[makeQuery(id+"F0.imprint","IMPRINT",EDGE,{"disambiguationData":[TD([[subQ2,-1.0]])],"derivedFrom":subQ1}),1.0]])]});}
            var Q74;
            {var subQ0=sQuery(id+"F0.wireOp",EDGE,"Sz0mojis-d1jk-JmHj-u71d-QuebyHLcdwvN.top");var subQ1=sQuery(id+"F0.wireOp",EDGE,"642ae80b-53ca-425f-9e1c-665031984c0c.left");var subQ2=makeQuery(id+"F0.imprint","INTERSECT",VERTEX,{"derivedFrom":[subQ1,subQ0]});Q74=makeQuery(id+"F0.imprint","IMPRINT",FACE,{"disambiguationData":[TD([[makeQuery(id+"F0.imprint","IMPRINT",EDGE,{"disambiguationData":[TD([[subQ2,-1.0]])],"derivedFrom":subQ1}),1.0]])]});}
            var Q75;
            {var subQ0=sQuery(id+"F0.wireOp",EDGE,"642ae80b-53ca-425f-9e1c-665031984c0c.left");var subQ1=sQuery(id+"F0.wireOp",EDGE,"642ae80b-53ca-425f-9e1c-665031984c0c.bottom");var subQ2=makeQuery(id+"F0.imprint","INTERSECT",VERTEX,{"derivedFrom":[subQ1,subQ0]});Q75=makeQuery(id+"F0.imprint","IMPRINT",FACE,{"disambiguationData":[TD([[makeQuery(id+"F0.imprint","IMPRINT",EDGE,{"disambiguationData":[TD([[subQ2,-1.0]])],"derivedFrom":subQ1}),-1.0]])]});}
            var Q76;
            {var subQ0=sQuery(id+"F0.wireOp",EDGE,"419c5b55-3d34-4837-8a7f-80514d8a6413.left");var subQ1=sQuery(id+"F0.wireOp",EDGE,"642ae80b-53ca-425f-9e1c-665031984c0c.bottom");var subQ2=makeQuery(id+"F0.imprint","INTERSECT",VERTEX,{"derivedFrom":[subQ1,subQ0]});Q76=makeQuery(id+"F0.imprint","IMPRINT",FACE,{"disambiguationData":[TD([[makeQuery(id+"F0.imprint","IMPRINT",EDGE,{"disambiguationData":[TD([[subQ2,-1.0]])],"derivedFrom":subQ1}),-1.0]])]});}
            var Q77;
            {var subQ0=sQuery(id+"F0.wireOp",EDGE,"642ae80b-53ca-425f-9e1c-665031984c0c.right");var subQ1=sQuery(id+"F0.wireOp",EDGE,"642ae80b-53ca-425f-9e1c-665031984c0c.bottom");var subQ2=makeQuery(id+"F0.imprint","INTERSECT",VERTEX,{"derivedFrom":[subQ1,subQ0]});Q77=makeQuery(id+"F0.imprint","IMPRINT",FACE,{"disambiguationData":[TD([[makeQuery(id+"F0.imprint","IMPRINT",EDGE,{"disambiguationData":[TD([[subQ2,1.0]])],"derivedFrom":subQ1}),-1.0]])]});}
            var Q78;
            {var subQ5=sQuery(id+"F0.wireOp",EDGE,"Sz0mojis-d1jk-JmHj-u71d-QuebyHLcdwvN.left");Q78=makeQuery(id+"F0.imprint","IMPRINT",FACE,{"disambiguationData":[TD([[makeQuery(id+"F0.imprint","IMPRINT",EDGE,{"derivedFrom":subQ5}),-1.0]])]});}
            var Q79;
            {var subQ0=sQuery(id+"F0.wireOp",EDGE,"YiqkaKLR-4Dmx-IN0i-HcmR-PsK4lVufwlE0.bottom");var subQ1=sQuery(id+"F0.wireOp",EDGE,"860cfe5d-25c9-4f5e-8e16-f1d030cc68f1.left");var subQ2=makeQuery(id+"F0.imprint","INTERSECT",VERTEX,{"derivedFrom":[subQ1,subQ0]});Q79=makeQuery(id+"F0.imprint","IMPRINT",FACE,{"disambiguationData":[TD([[makeQuery(id+"F0.imprint","IMPRINT",EDGE,{"disambiguationData":[TD([[subQ2,-1.0]])],"derivedFrom":subQ1}),-1.0]])]});}
            var Q80;
            {var subQ5=sQuery(id+"F0.wireOp",EDGE,"426b8349-3ba2-487a-b433-ea0838ed4720.right");Q80=makeQuery(id+"F0.imprint","IMPRINT",FACE,{"disambiguationData":[TD([[makeQuery(id+"F0.imprint","IMPRINT",EDGE,{"derivedFrom":subQ5}),-1.0]])]});}
            var Q81;
            {var subQ0=sQuery(id+"F0.wireOp",EDGE,"f06d2eca-08b4-4a93-9f64-039db08a78e3.left");var subQ1=sQuery(id+"F0.wireOp",EDGE,"426b8349-3ba2-487a-b433-ea0838ed4720.top");var subQ2=makeQuery(id+"F0.imprint","INTERSECT",VERTEX,{"derivedFrom":[subQ1,subQ0]});Q81=makeQuery(id+"F0.imprint","IMPRINT",FACE,{"disambiguationData":[TD([[makeQuery(id+"F0.imprint","IMPRINT",EDGE,{"disambiguationData":[TD([[subQ2,-1.0]])],"derivedFrom":subQ1}),1.0]])]});}
            var Q82;
            {var subQ5=sQuery(id+"F0.wireOp",EDGE,"94d76ea6-7cc8-4181-b856-171572913172.left");Q82=makeQuery(id+"F0.imprint","IMPRINT",FACE,{"disambiguationData":[TD([[makeQuery(id+"F0.imprint","IMPRINT",EDGE,{"derivedFrom":subQ5}),-1.0]])]});}
            var Q83;
            {var subQ0=sQuery(id+"F0.wireOp",EDGE,"a0c58bf9-3c41-4803-aa84-dba70619896c");Q83=makeQuery(id+"F0.imprint","IMPRINT",FACE,{"disambiguationData":[TD([[makeQuery(id+"F0.imprint","IMPRINT",EDGE,{"derivedFrom":subQ0}),1.0]])]});}
            var Q84;
            {var subQ5=sQuery(id+"F0.wireOp",EDGE,"f06d2eca-08b4-4a93-9f64-039db08a78e3.top");Q84=makeQuery(id+"F0.imprint","IMPRINT",FACE,{"disambiguationData":[TD([[makeQuery(id+"F0.imprint","IMPRINT",EDGE,{"derivedFrom":subQ5}),-1.0]])]});}
            var Q85;
            {var subQ0=sQuery(id+"F0.wireOp",EDGE,"Sz0mojis-d1jk-JmHj-u71d-QuebyHLcdwvN.bottom");var subQ1=sQuery(id+"F0.wireOp",EDGE,"419c5b55-3d34-4837-8a7f-80514d8a6413.left");var subQ2=makeQuery(id+"F0.imprint","INTERSECT",VERTEX,{"derivedFrom":[subQ1,subQ0]});Q85=makeQuery(id+"F0.imprint","IMPRINT",FACE,{"disambiguationData":[TD([[makeQuery(id+"F0.imprint","IMPRINT",EDGE,{"disambiguationData":[TD([[subQ2,-1.0]])],"derivedFrom":subQ1}),-1.0]])]});}
            var Q86;
            {var subQ5=sQuery(id+"F0.wireOp",EDGE,"f06d2eca-08b4-4a93-9f64-039db08a78e3.bottom");Q86=makeQuery(id+"F0.imprint","IMPRINT",FACE,{"disambiguationData":[TD([[makeQuery(id+"F0.imprint","IMPRINT",EDGE,{"derivedFrom":subQ5}),1.0]])]});}
            var Q87;
            {var subQ5=sQuery(id+"F0.wireOp",EDGE,"94d76ea6-7cc8-4181-b856-171572913172.right");Q87=makeQuery(id+"F0.imprint","IMPRINT",FACE,{"disambiguationData":[TD([[makeQuery(id+"F0.imprint","IMPRINT",EDGE,{"derivedFrom":subQ5}),1.0]])]});}
            var Q88;
            {var subQ0=sQuery(id+"F0.wireOp",EDGE,"Sz0mojis-d1jk-JmHj-u71d-QuebyHLcdwvN.bottom");var subQ1=sQuery(id+"F0.wireOp",EDGE,"419c5b55-3d34-4837-8a7f-80514d8a6413.left");var subQ2=makeQuery(id+"F0.imprint","INTERSECT",VERTEX,{"derivedFrom":[subQ1,subQ0]});Q88=makeQuery(id+"F0.imprint","IMPRINT",FACE,{"disambiguationData":[TD([[makeQuery(id+"F0.imprint","IMPRINT",EDGE,{"disambiguationData":[TD([[subQ2,-1.0]])],"derivedFrom":subQ1}),-1.0]])]});}
            var Q89;
            {var subQ0=sQuery(id+"F0.wireOp",EDGE,"Sz0mojis-d1jk-JmHj-u71d-QuebyHLcdwvN.top");var subQ1=sQuery(id+"F0.wireOp",EDGE,"642ae80b-53ca-425f-9e1c-665031984c0c.right");var subQ2=makeQuery(id+"F0.imprint","INTERSECT",VERTEX,{"derivedFrom":[subQ1,subQ0]});Q89=makeQuery(id+"F0.imprint","IMPRINT",FACE,{"disambiguationData":[TD([[makeQuery(id+"F0.imprint","IMPRINT",EDGE,{"disambiguationData":[TD([[subQ2,-1.0]])],"derivedFrom":subQ1}),-1.0]])]});}
            var Q90;
            {var subQ1=sQuery(id+"F0.wireOp",EDGE,"9QrijVwn-rOgx-UGeQ-xbAQ-nRElRZnjGxsu.bottom");Q90=makeQuery(id+"F0.imprint","IMPRINT",FACE,{"disambiguationData":[TD([[makeQuery(id+"F0.imprint","IMPRINT",EDGE,{"derivedFrom":subQ1}),1.0]])]});}
            var Q91;
            {var subQ0=sQuery(id+"F0.wireOp",EDGE,"57e6ceb0-2b07-4070-b827-d5ddd958e3c5");var subQ1=sQuery(id+"F0.wireOp",EDGE,"50b46a36-ce94-46d7-8646-d56a16b42dbd.bottom");var subQ2=makeQuery(id+"F0.imprint","INTERSECT",VERTEX,{"derivedFrom":[subQ1,subQ0]});Q91=makeQuery(id+"F0.imprint","IMPRINT",FACE,{"disambiguationData":[TD([[makeQuery(id+"F0.imprint","IMPRINT",EDGE,{"disambiguationData":[TD([[subQ2,-1.0]])],"derivedFrom":subQ1}),-1.0]])]});}
            var Q92;
            {var subQ0=sQuery(id+"F0.wireOp",EDGE,"57e6ceb0-2b07-4070-b827-d5ddd958e3c5");var subQ1=sQuery(id+"F0.wireOp",EDGE,"50b46a36-ce94-46d7-8646-d56a16b42dbd.bottom");var subQ2=makeQuery(id+"F0.imprint","INTERSECT",VERTEX,{"derivedFrom":[subQ1,subQ0]});Q92=makeQuery(id+"F0.imprint","IMPRINT",FACE,{"disambiguationData":[TD([[makeQuery(id+"F0.imprint","IMPRINT",EDGE,{"disambiguationData":[TD([[subQ2,1.0]])],"derivedFrom":subQ1}),-1.0]])]});}
            var Q93;
            {var subQ0=sQuery(id+"F0.wireOp",EDGE,"3d998c80-86e5-4b8b-905e-37de4b0267f5");Q93=makeQuery(id+"F0.imprint","IMPRINT",FACE,{"disambiguationData":[TD([[makeQuery(id+"F0.imprint","IMPRINT",EDGE,{"derivedFrom":subQ0}),1.0]])]});}
            var Q94;
            {var subQ5=sQuery(id+"F0.wireOp",EDGE,"Sz0mojis-d1jk-JmHj-u71d-QuebyHLcdwvN.right");Q94=makeQuery(id+"F0.imprint","IMPRINT",FACE,{"disambiguationData":[TD([[makeQuery(id+"F0.imprint","IMPRINT",EDGE,{"derivedFrom":subQ5}),1.0]])]});}
            var Q95;
            {var subQ5=sQuery(id+"F0.wireOp",EDGE,"419c5b55-3d34-4837-8a7f-80514d8a6413.top");Q95=makeQuery(id+"F0.imprint","IMPRINT",FACE,{"disambiguationData":[TD([[makeQuery(id+"F0.imprint","IMPRINT",EDGE,{"derivedFrom":subQ5}),-1.0]])]});}
            var Q96;
            {var subQ5=sQuery(id+"F0.wireOp",EDGE,"419c5b55-3d34-4837-8a7f-80514d8a6413.bottom");Q96=makeQuery(id+"F0.imprint","IMPRINT",FACE,{"disambiguationData":[TD([[makeQuery(id+"F0.imprint","IMPRINT",EDGE,{"derivedFrom":subQ5}),1.0]])]});}
            var Q97;
            {var subQ5=sQuery(id+"F0.wireOp",EDGE,"YiqkaKLR-4Dmx-IN0i-HcmR-PsK4lVufwlE0.right");Q97=makeQuery(id+"F0.imprint","IMPRINT",FACE,{"disambiguationData":[TD([[makeQuery(id+"F0.imprint","IMPRINT",EDGE,{"derivedFrom":subQ5}),1.0]])]});}
            var Q98;
            {var subQ0=sQuery(id+"F0.wireOp",EDGE,"f06d2eca-08b4-4a93-9f64-039db08a78e3.left");var subQ1=sQuery(id+"F0.wireOp",EDGE,"426b8349-3ba2-487a-b433-ea0838ed4720.bottom");var subQ2=makeQuery(id+"F0.imprint","INTERSECT",VERTEX,{"derivedFrom":[subQ1,subQ0]});Q98=makeQuery(id+"F0.imprint","IMPRINT",FACE,{"disambiguationData":[TD([[makeQuery(id+"F0.imprint","IMPRINT",EDGE,{"disambiguationData":[TD([[subQ2,-1.0]])],"derivedFrom":subQ1}),-1.0]])]});}
            var Q99;
            {var subQ0=sQuery(id+"F0.wireOp",EDGE,"94d76ea6-7cc8-4181-b856-171572913172.bottom");var subQ1=sQuery(id+"F0.wireOp",EDGE,"f06d2eca-08b4-4a93-9f64-039db08a78e3.left");var subQ2=makeQuery(id+"F0.imprint","INTERSECT",VERTEX,{"derivedFrom":[subQ1,subQ0]});Q99=makeQuery(id+"F0.imprint","IMPRINT",FACE,{"disambiguationData":[TD([[makeQuery(id+"F0.imprint","IMPRINT",EDGE,{"disambiguationData":[TD([[subQ2,-1.0]])],"derivedFrom":subQ1}),-1.0]])]});}
            var Q100;
            Q100=makeQuery(id+"F0.imprint","IMPRINT",FACE,{"disambiguationData":[TD([[makeQuery(id+"F0.imprint","IMPRINT",EDGE,{"derivedFrom":sQuery(id+"F0.wireOp",EDGE,"E69.bottom")}),-1.0]])]});
            var Q101;
            {var subQ0=sQuery(id+"F0.wireOp",EDGE,"WO7FBR6K-NqwA-dO00-k5Az-VCm2GtCYNAmY.top");Q101=makeQuery(id+"F0.imprint","IMPRINT",FACE,{"disambiguationData":[TD([[makeQuery(id+"F0.imprint","IMPRINT",EDGE,{"derivedFrom":subQ0}),1.0]])]});}
            var Q102;
            {var subQ5=sQuery(id+"F0.wireOp",EDGE,"WO7FBR6K-NqwA-dO00-k5Az-VCm2GtCYNAmY.top");Q102=makeQuery(id+"F0.imprint","IMPRINT",FACE,{"disambiguationData":[TD([[makeQuery(id+"F0.imprint","IMPRINT",EDGE,{"derivedFrom":subQ5}),-1.0]])]});}
            var Q103;
            {var subQ0=sQuery(id+"F0.wireOp",EDGE,"uv323xyt-ov5L-Y3er-0I5r-GefFz3S0IUKK");Q103=makeQuery(id+"F0.imprint","IMPRINT",FACE,{"disambiguationData":[TD([[makeQuery(id+"F0.imprint","IMPRINT",EDGE,{"derivedFrom":subQ0}),1.0]])]});}
            var Q104;
            {var subQ4=sQuery(id+"F0.wireOp",EDGE,"Nd1QmWF3-HgH3-pVPl-pdns-4euAvYWHRr2N");Q104=makeQuery(id+"F0.imprint","IMPRINT",FACE,{"disambiguationData":[TD([[makeQuery(id+"F0.imprint","IMPRINT",EDGE,{"derivedFrom":subQ4}),1.0]])]});}
            var Q105;
            {var subQ0=sQuery(id+"F0.wireOp",EDGE,"Nd1QmWF3-HgH3-pVPl-pdns-4euAvYWHRr2N");Q105=makeQuery(id+"F0.imprint","IMPRINT",FACE,{"disambiguationData":[TD([[makeQuery(id+"F0.imprint","IMPRINT",EDGE,{"derivedFrom":subQ0}),-1.0]])]});}
            var Q106;
            {var subQ0=sQuery(id+"F0.wireOp",EDGE,"BqNXshhi-u7Yk-G1wr-J3Ll-iod1uzp0lzdt");Q106=makeQuery(id+"F0.imprint","IMPRINT",FACE,{"disambiguationData":[TD([[makeQuery(id+"F0.imprint","IMPRINT",EDGE,{"derivedFrom":subQ0}),1.0]])]});}
            var Q107;
            {var subQ0=sQuery(id+"F0.wireOp",EDGE,"fM8DBSm8-YZ9Q-zzWP-7De2-ZU5yQOtgJdYL");Q107=makeQuery(id+"F0.imprint","IMPRINT",FACE,{"disambiguationData":[TD([[makeQuery(id+"F0.imprint","IMPRINT",EDGE,{"derivedFrom":subQ0}),-1.0]])]});}
            var Q108;
            {var subQ3=sQuery(id+"F0.wireOp",EDGE,"fM8DBSm8-YZ9Q-zzWP-7De2-ZU5yQOtgJdYL");Q108=makeQuery(id+"F0.imprint","IMPRINT",FACE,{"disambiguationData":[TD([[makeQuery(id+"F0.imprint","IMPRINT",EDGE,{"derivedFrom":subQ3}),1.0]])]});}
            var Q109;
            {var subQ5=sQuery(id+"F0.wireOp",EDGE,"97bzH4Fx-8Kzi-5AMC-lFeI-Fmnh76GxepJg.right");Q109=makeQuery(id+"F0.imprint","IMPRINT",FACE,{"disambiguationData":[TD([[makeQuery(id+"F0.imprint","IMPRINT",EDGE,{"derivedFrom":subQ5}),-1.0]])]});}
            var Q110;
            {var subQ5=sQuery(id+"F0.wireOp",EDGE,"A6C4znJQ-Hph2-yxI6-4gdU-WQJ5AQLR1BA1.right");Q110=makeQuery(id+"F0.imprint","IMPRINT",FACE,{"disambiguationData":[TD([[makeQuery(id+"F0.imprint","IMPRINT",EDGE,{"derivedFrom":subQ5}),1.0]])]});}
            var Q111;
            {var subQ0=sQuery(id+"F0.wireOp",EDGE,"3CZl91N5-HSj3-Hn57-O96J-kGScyooqo1bc");Q111=makeQuery(id+"F0.imprint","IMPRINT",FACE,{"disambiguationData":[TD([[makeQuery(id+"F0.imprint","IMPRINT",EDGE,{"derivedFrom":subQ0}),1.0]])]});}
            var Q112;
            {var subQ5=sQuery(id+"F0.wireOp",EDGE,"DNnriFE3-ud94-ZcwE-caHn-EOKIcGiwGioX.top");Q112=makeQuery(id+"F0.imprint","IMPRINT",FACE,{"disambiguationData":[TD([[makeQuery(id+"F0.imprint","IMPRINT",EDGE,{"derivedFrom":subQ5}),1.0]])]});}
            var Q113;
            {var subQ5=sQuery(id+"F0.wireOp",EDGE,"DNnriFE3-ud94-ZcwE-caHn-EOKIcGiwGioX.bottom");Q113=makeQuery(id+"F0.imprint","IMPRINT",FACE,{"disambiguationData":[TD([[makeQuery(id+"F0.imprint","IMPRINT",EDGE,{"derivedFrom":subQ5}),-1.0]])]});}
            var Q114;
            {var subQ0=sQuery(id+"F0.wireOp",EDGE,"4DcOnRe5-BHuk-WRBC-3sxB-7I3lZaO44Omp");Q114=makeQuery(id+"F0.imprint","IMPRINT",FACE,{"disambiguationData":[TD([[makeQuery(id+"F0.imprint","IMPRINT",EDGE,{"derivedFrom":subQ0}),-1.0]])]});}
            var Q115;
            {var subQ3=sQuery(id+"F0.wireOp",EDGE,"425e234b-cbbb-423d-ba30-d765a685e7fc");Q115=makeQuery(id+"F0.imprint","IMPRINT",FACE,{"disambiguationData":[TD([[makeQuery(id+"F0.imprint","IMPRINT",EDGE,{"derivedFrom":subQ3}),1.0]])]});}
            var Q116;
            {var subQ0=sQuery(id+"F0.wireOp",EDGE,"425e234b-cbbb-423d-ba30-d765a685e7fc");Q116=makeQuery(id+"F0.imprint","IMPRINT",FACE,{"disambiguationData":[TD([[makeQuery(id+"F0.imprint","IMPRINT",EDGE,{"derivedFrom":subQ0}),-1.0]])]});}
            var Q117;
            {var subQ0=sQuery(id+"F0.wireOp",EDGE,"be1eab0f-760e-4d8a-837a-be46e0181c46");Q117=makeQuery(id+"F0.imprint","IMPRINT",FACE,{"disambiguationData":[TD([[makeQuery(id+"F0.imprint","IMPRINT",EDGE,{"derivedFrom":subQ0}),1.0]])]});}
            var Q118;
            {var subQ4=sQuery(id+"F0.wireOp",EDGE,"18a23e4c-a506-405f-9391-233385794a7d");Q118=makeQuery(id+"F0.imprint","IMPRINT",FACE,{"disambiguationData":[TD([[makeQuery(id+"F0.imprint","IMPRINT",EDGE,{"derivedFrom":subQ4}),1.0]])]});}
            var Q119;
            {var subQ1=sQuery(id+"F0.wireOp",EDGE,"a7da8269-c69e-4b82-a0b7-ee7e832f81cc.top");Q119=makeQuery(id+"F0.imprint","IMPRINT",FACE,{"disambiguationData":[TD([[makeQuery(id+"F0.imprint","IMPRINT",EDGE,{"derivedFrom":subQ1}),1.0]])]});}
            var Q120;
            {var subQ0=sQuery(id+"F0.wireOp",EDGE,"0b1762db-f3ff-4d00-8078-3d92d6001052");Q120=makeQuery(id+"F0.imprint","IMPRINT",FACE,{"disambiguationData":[TD([[makeQuery(id+"F0.imprint","IMPRINT",EDGE,{"derivedFrom":subQ0}),1.0]])]});}
            var Q121;
            {var subQ0=sQuery(id+"F0.wireOp",EDGE,"18a23e4c-a506-405f-9391-233385794a7d");Q121=makeQuery(id+"F0.imprint","IMPRINT",FACE,{"disambiguationData":[TD([[makeQuery(id+"F0.imprint","IMPRINT",EDGE,{"derivedFrom":subQ0}),-1.0]])]});}
            var Q122;
            {var subQ5=sQuery(id+"F0.wireOp",EDGE,"ca78b25e-4be0-47e7-a1ed-f3240bc97c62.right");Q122=makeQuery(id+"F0.imprint","IMPRINT",FACE,{"disambiguationData":[TD([[makeQuery(id+"F0.imprint","IMPRINT",EDGE,{"derivedFrom":subQ5}),-1.0]])]});}
            var Q123;
            {var subQ5=sQuery(id+"F0.wireOp",EDGE,"dc8c2f64-a6d5-4961-a0ce-f4d6bab24f91.right");Q123=makeQuery(id+"F0.imprint","IMPRINT",FACE,{"disambiguationData":[TD([[makeQuery(id+"F0.imprint","IMPRINT",EDGE,{"derivedFrom":subQ5}),1.0]])]});}
            var Q124;
            {var subQ0=sQuery(id+"F0.wireOp",EDGE,"1e36d728-9d9d-4a0f-8e68-62208997cefa");Q124=makeQuery(id+"F0.imprint","IMPRINT",FACE,{"disambiguationData":[TD([[makeQuery(id+"F0.imprint","IMPRINT",EDGE,{"derivedFrom":subQ0}),1.0]])]});}
            var Q125;
            {var subQ0=sQuery(id+"F0.wireOp",EDGE,"3402ff42-d9ce-4f8e-9a3a-d90509ac5dec");Q125=makeQuery(id+"F0.imprint","IMPRINT",FACE,{"disambiguationData":[TD([[makeQuery(id+"F0.imprint","IMPRINT",EDGE,{"derivedFrom":subQ0}),-1.0]])]});}
            var Q126;
            {var subQ5=sQuery(id+"F0.wireOp",EDGE,"63f710fc-a6c8-4fb9-b046-ab74eb3c5c8b.top");Q126=makeQuery(id+"F0.imprint","IMPRINT",FACE,{"disambiguationData":[TD([[makeQuery(id+"F0.imprint","IMPRINT",EDGE,{"derivedFrom":subQ5}),1.0]])]});}
            var Q127;
            {var subQ5=sQuery(id+"F0.wireOp",EDGE,"63f710fc-a6c8-4fb9-b046-ab74eb3c5c8b.bottom");Q127=makeQuery(id+"F0.imprint","IMPRINT",FACE,{"disambiguationData":[TD([[makeQuery(id+"F0.imprint","IMPRINT",EDGE,{"derivedFrom":subQ5}),-1.0]])]});}
            var Q128;
            {var subQ3=sQuery(id+"F0.wireOp",EDGE,"a3f150c6-0f1f-4b2c-a122-f7c8c5175d6d");Q128=makeQuery(id+"F0.imprint","IMPRINT",FACE,{"disambiguationData":[TD([[makeQuery(id+"F0.imprint","IMPRINT",EDGE,{"derivedFrom":subQ3}),1.0]])]});}
            var Q129;
            {var subQ0=sQuery(id+"F0.wireOp",EDGE,"77baf98d-4ae9-472d-b08e-ad650eed60c0");Q129=makeQuery(id+"F0.imprint","IMPRINT",FACE,{"disambiguationData":[TD([[makeQuery(id+"F0.imprint","IMPRINT",EDGE,{"derivedFrom":subQ0}),1.0]])]});}
            var Q130;
            {var subQ0=sQuery(id+"F0.wireOp",EDGE,"a3f150c6-0f1f-4b2c-a122-f7c8c5175d6d");Q130=makeQuery(id+"F0.imprint","IMPRINT",FACE,{"disambiguationData":[TD([[makeQuery(id+"F0.imprint","IMPRINT",EDGE,{"derivedFrom":subQ0}),-1.0]])]});}
            var Q131;
            {var subQ0=sQuery(id+"F0.wireOp",EDGE,"1687e972-166c-4726-a24b-8a66f6d2e850");Q131=makeQuery(id+"F0.imprint","IMPRINT",FACE,{"disambiguationData":[TD([[makeQuery(id+"F0.imprint","IMPRINT",EDGE,{"derivedFrom":subQ0}),1.0]])]});}
            var Q132;
            {var subQ4=sQuery(id+"F0.wireOp",EDGE,"567b0da1-2da1-43b4-8e98-518e5b8e30c9");Q132=makeQuery(id+"F0.imprint","IMPRINT",FACE,{"disambiguationData":[TD([[makeQuery(id+"F0.imprint","IMPRINT",EDGE,{"derivedFrom":subQ4}),1.0]])]});}
            var Q133;
            {var subQ0=sQuery(id+"F0.wireOp",EDGE,"567b0da1-2da1-43b4-8e98-518e5b8e30c9");Q133=makeQuery(id+"F0.imprint","IMPRINT",FACE,{"disambiguationData":[TD([[makeQuery(id+"F0.imprint","IMPRINT",EDGE,{"derivedFrom":subQ0}),-1.0]])]});}
            var Q134;
            {var subQ0=sQuery(id+"F0.wireOp",EDGE,"1698c45c-fd21-4e88-85cb-be6a72ba41c8");Q134=makeQuery(id+"F0.imprint","IMPRINT",FACE,{"disambiguationData":[TD([[makeQuery(id+"F0.imprint","IMPRINT",EDGE,{"derivedFrom":subQ0}),1.0]])]});}
            var Q135;
            {var subQ3=sQuery(id+"F0.wireOp",EDGE,"79670a96-043d-493e-ab2a-8d6fa8f5f1ac");Q135=makeQuery(id+"F0.imprint","IMPRINT",FACE,{"disambiguationData":[TD([[makeQuery(id+"F0.imprint","IMPRINT",EDGE,{"derivedFrom":subQ3}),1.0]])]});}
            var Q136;
            {var subQ0=sQuery(id+"F0.wireOp",EDGE,"79670a96-043d-493e-ab2a-8d6fa8f5f1ac");Q136=makeQuery(id+"F0.imprint","IMPRINT",FACE,{"disambiguationData":[TD([[makeQuery(id+"F0.imprint","IMPRINT",EDGE,{"derivedFrom":subQ0}),-1.0]])]});}
            var Q137;
            {var subQ0=sQuery(id+"F0.wireOp",EDGE,"2e6bfe16-f223-435e-b6a1-06214fae2e31");Q137=makeQuery(id+"F0.imprint","IMPRINT",FACE,{"disambiguationData":[TD([[makeQuery(id+"F0.imprint","IMPRINT",EDGE,{"derivedFrom":subQ0}),1.0]])]});}
            var Q138;
            {var subQ4=sQuery(id+"F0.wireOp",EDGE,"b942833b-3975-4883-b875-2b67912b20ac");Q138=makeQuery(id+"F0.imprint","IMPRINT",FACE,{"disambiguationData":[TD([[makeQuery(id+"F0.imprint","IMPRINT",EDGE,{"derivedFrom":subQ4}),1.0]])]});}
            var Q139;
            {var subQ0=sQuery(id+"F0.wireOp",EDGE,"b942833b-3975-4883-b875-2b67912b20ac");Q139=makeQuery(id+"F0.imprint","IMPRINT",FACE,{"disambiguationData":[TD([[makeQuery(id+"F0.imprint","IMPRINT",EDGE,{"derivedFrom":subQ0}),-1.0]])]});}
            var Q140;
            {var subQ1=sQuery(id+"F0.wireOp",EDGE,"2e51a8b0-1f03-4952-93e3-02f89a284ef5.top");Q140=makeQuery(id+"F0.imprint","IMPRINT",FACE,{"disambiguationData":[TD([[makeQuery(id+"F0.imprint","IMPRINT",EDGE,{"derivedFrom":subQ1}),1.0]])]});}
            var Q141;
            {var subQ5=sQuery(id+"F0.wireOp",EDGE,"d4461469-d64e-4703-8aa8-f203ecc49780.right");Q141=makeQuery(id+"F0.imprint","IMPRINT",FACE,{"disambiguationData":[TD([[makeQuery(id+"F0.imprint","IMPRINT",EDGE,{"derivedFrom":subQ5}),-1.0]])]});}
            var Q142;
            {var subQ5=sQuery(id+"F0.wireOp",EDGE,"2e51a8b0-1f03-4952-93e3-02f89a284ef5.top");Q142=makeQuery(id+"F0.imprint","IMPRINT",FACE,{"disambiguationData":[TD([[makeQuery(id+"F0.imprint","IMPRINT",EDGE,{"derivedFrom":subQ5}),-1.0]])]});}
            var Q143;
            {var subQ5=sQuery(id+"F0.wireOp",EDGE,"d0fb6f9a-522a-4aa1-a7c2-23e37d4c0213.right");Q143=makeQuery(id+"F0.imprint","IMPRINT",FACE,{"disambiguationData":[TD([[makeQuery(id+"F0.imprint","IMPRINT",EDGE,{"derivedFrom":subQ5}),1.0]])]});}
            var Q144;
            {var subQ5=sQuery(id+"F0.wireOp",EDGE,"53508f4b-f4cb-45eb-a756-4067c27c1d39.top");Q144=makeQuery(id+"F0.imprint","IMPRINT",FACE,{"disambiguationData":[TD([[makeQuery(id+"F0.imprint","IMPRINT",EDGE,{"derivedFrom":subQ5}),1.0]])]});}
            var Q145;
            {var subQ5=sQuery(id+"F0.wireOp",EDGE,"a7da8269-c69e-4b82-a0b7-ee7e832f81cc.top");Q145=makeQuery(id+"F0.imprint","IMPRINT",FACE,{"disambiguationData":[TD([[makeQuery(id+"F0.imprint","IMPRINT",EDGE,{"derivedFrom":subQ5}),-1.0]])]});}
            var Q146;
            {var subQ1=sQuery(id+"F0.wireOp",EDGE,"06Dy8Mhb-cmLM-6IrH-Xf5E-i4oV1XNrsM1v.bottom");var subQ3=sQuery(id+"F0.wireOp",EDGE,"kxZD4Upu-KWbA-6jD0-Vrha-qKam3SFhEEaQ");var subQ4=makeQuery(id+"F0.imprint","INTERSECT",VERTEX,{"derivedFrom":[subQ1,subQ3]});Q146=makeQuery(id+"F0.imprint","IMPRINT",FACE,{"disambiguationData":[TD([[makeQuery(id+"F0.imprint","IMPRINT",EDGE,{"disambiguationData":[TD([[subQ4,1.0]])],"derivedFrom":subQ1}),1.0]])]});}
            var Q147;
            {var subQ5=sQuery(id+"F0.wireOp",EDGE,"p9fGJ3IM-FqPl-Tcoq-nwBU-R3OxuuyoPV2a.top");var subQ7=sQuery(id+"F0.wireOp",EDGE,"ec82b42a-04d0-48a3-93bc-dfdf67d3ded2.right");var subQ8=makeQuery(id+"F0.imprint","INTERSECT",VERTEX,{"derivedFrom":[subQ7,subQ5]});Q147=makeQuery(id+"F0.imprint","IMPRINT",FACE,{"disambiguationData":[TD([[makeQuery(id+"F0.imprint","IMPRINT",EDGE,{"disambiguationData":[TD([[subQ8,-1.0]])],"derivedFrom":subQ7}),1.0]])]});}
            var Q148;
            {var subQ1=sQuery(id+"F0.wireOp",EDGE,"ec82b42a-04d0-48a3-93bc-dfdf67d3ded2.top");var subQ3=sQuery(id+"F0.wireOp",EDGE,"UhtWTb3c-HlOh-6Js7-5CIq-PquVUd3KIVgp.right");var subQ4=makeQuery(id+"F0.imprint","INTERSECT",VERTEX,{"derivedFrom":[subQ1,subQ3]});Q148=makeQuery(id+"F0.imprint","IMPRINT",FACE,{"disambiguationData":[TD([[makeQuery(id+"F0.imprint","IMPRINT",EDGE,{"disambiguationData":[TD([[subQ4,-1.0]])],"derivedFrom":subQ3}),1.0]])]});}
            var Q149;
            {var subQ1=sQuery(id+"F0.wireOp",EDGE,"ec82b42a-04d0-48a3-93bc-dfdf67d3ded2.top");var subQ3=sQuery(id+"F0.wireOp",EDGE,"UhtWTb3c-HlOh-6Js7-5CIq-PquVUd3KIVgp.left");var subQ4=makeQuery(id+"F0.imprint","INTERSECT",VERTEX,{"derivedFrom":[subQ1,subQ3]});Q149=makeQuery(id+"F0.imprint","IMPRINT",FACE,{"disambiguationData":[TD([[makeQuery(id+"F0.imprint","IMPRINT",EDGE,{"disambiguationData":[TD([[subQ4,-1.0]])],"derivedFrom":subQ3}),-1.0]])]});}
            var Q150;
            {var subQ22=sQuery(id+"F0.wireOp",EDGE,"UhtWTb3c-HlOh-6Js7-5CIq-PquVUd3KIVgp.bottom");Q150=makeQuery(id+"F0.imprint","IMPRINT",FACE,{"disambiguationData":[TD([[makeQuery(id+"F0.imprint","IMPRINT",EDGE,{"derivedFrom":subQ22}),1.0]])]});}
            var Q151;
            {var subQ5=sQuery(id+"F0.wireOp",EDGE,"UhtWTb3c-HlOh-6Js7-5CIq-PquVUd3KIVgp.bottom");Q151=makeQuery(id+"F0.imprint","IMPRINT",FACE,{"disambiguationData":[TD([[makeQuery(id+"F0.imprint","IMPRINT",EDGE,{"derivedFrom":subQ5}),-1.0]])]});}
            var Q152;
            {var subQ1=sQuery(id+"F0.wireOp",EDGE,"ec82b42a-04d0-48a3-93bc-dfdf67d3ded2.left");var subQ3=sQuery(id+"F0.wireOp",EDGE,"NntFXoqW-AxeH-TwTq-xJpQ-qcDSb9PKY8J3.top");var subQ4=makeQuery(id+"F0.imprint","INTERSECT",VERTEX,{"derivedFrom":[subQ1,subQ3]});Q152=makeQuery(id+"F0.imprint","IMPRINT",FACE,{"disambiguationData":[TD([[makeQuery(id+"F0.imprint","IMPRINT",EDGE,{"disambiguationData":[TD([[subQ4,-1.0]])],"derivedFrom":subQ1}),-1.0]])]});}
            var Q153;
            {var subQ1=sQuery(id+"F0.wireOp",EDGE,"06Dy8Mhb-cmLM-6IrH-Xf5E-i4oV1XNrsM1v.bottom");var subQ3=sQuery(id+"F0.wireOp",EDGE,"4bZdnYDA-Iz10-3bQz-BeRK-vAqJ3djD3Fpo");var subQ4=makeQuery(id+"F0.imprint","INTERSECT",VERTEX,{"derivedFrom":[subQ1,subQ3]});Q153=makeQuery(id+"F0.imprint","IMPRINT",FACE,{"disambiguationData":[TD([[makeQuery(id+"F0.imprint","IMPRINT",EDGE,{"disambiguationData":[TD([[subQ4,-1.0]])],"derivedFrom":subQ1}),1.0]])]});}
            var Q154;
            {var subQ5=sQuery(id+"F0.wireOp",EDGE,"p9fGJ3IM-FqPl-Tcoq-nwBU-R3OxuuyoPV2a.right");Q154=makeQuery(id+"F0.imprint","IMPRINT",FACE,{"disambiguationData":[TD([[makeQuery(id+"F0.imprint","IMPRINT",EDGE,{"derivedFrom":subQ5}),1.0]])]});}
            var Q155;
            {var subQ5=sQuery(id+"F0.wireOp",EDGE,"NntFXoqW-AxeH-TwTq-xJpQ-qcDSb9PKY8J3.right");Q155=makeQuery(id+"F0.imprint","IMPRINT",FACE,{"disambiguationData":[TD([[makeQuery(id+"F0.imprint","IMPRINT",EDGE,{"derivedFrom":subQ5}),-1.0]])]});}
            var Q156;
            {var subQ5=sQuery(id+"F0.wireOp",EDGE,"0qXocB6W-gsSV-PXse-HaPV-ISHZLgC5pbNE.top");Q156=makeQuery(id+"F0.imprint","IMPRINT",FACE,{"disambiguationData":[TD([[makeQuery(id+"F0.imprint","IMPRINT",EDGE,{"derivedFrom":subQ5}),1.0]])]});}
            var Q157;
            {var subQ5=sQuery(id+"F0.wireOp",EDGE,"0qXocB6W-gsSV-PXse-HaPV-ISHZLgC5pbNE.bottom");Q157=makeQuery(id+"F0.imprint","IMPRINT",FACE,{"disambiguationData":[TD([[makeQuery(id+"F0.imprint","IMPRINT",EDGE,{"derivedFrom":subQ5}),-1.0]])]});}
            var Q158;
            {var subQ3=sQuery(id+"F0.wireOp",EDGE,"hDNJxt9Q-jmvS-7SMI-BvZw-ImVPGCuex0wg");Q158=makeQuery(id+"F0.imprint","IMPRINT",FACE,{"disambiguationData":[TD([[makeQuery(id+"F0.imprint","IMPRINT",EDGE,{"derivedFrom":subQ3}),-1.0]])]});}
            var Q159;
            {var subQ3=sQuery(id+"F0.wireOp",EDGE,"yFKCHMks-5PYb-OFws-e4Zj-Am98Z0KufoIo");Q159=makeQuery(id+"F0.imprint","IMPRINT",FACE,{"disambiguationData":[TD([[makeQuery(id+"F0.imprint","IMPRINT",EDGE,{"derivedFrom":subQ3}),1.0]])]});}
            var Q160;
            {var subQ0=sQuery(id+"F0.wireOp",EDGE,"CG18HeuL-z9TT-mQFl-Qw3X-3c35D3t7SPZm.right");Q160=makeQuery(id+"F0.imprint","IMPRINT",FACE,{"disambiguationData":[TD([[makeQuery(id+"F0.imprint","IMPRINT",EDGE,{"derivedFrom":subQ0}),1.0]])]});}
            var Q161;
            {var subQ5=sQuery(id+"F0.wireOp",EDGE,"IF45TSdG-J9Qy-20L9-T7Qw-abYBFXsGQqli.right");Q161=makeQuery(id+"F0.imprint","IMPRINT",FACE,{"disambiguationData":[TD([[makeQuery(id+"F0.imprint","IMPRINT",EDGE,{"derivedFrom":subQ5}),1.0]])]});}
            var Q162;
            {var subQ5=sQuery(id+"F0.wireOp",EDGE,"CG18HeuL-z9TT-mQFl-Qw3X-3c35D3t7SPZm.right");Q162=makeQuery(id+"F0.imprint","IMPRINT",FACE,{"disambiguationData":[TD([[makeQuery(id+"F0.imprint","IMPRINT",EDGE,{"derivedFrom":subQ5}),-1.0]])]});}
            var Q163;
            {var subQ5=sQuery(id+"F0.wireOp",EDGE,"IF45TSdG-J9Qy-20L9-T7Qw-abYBFXsGQqli.right");Q163=makeQuery(id+"F0.imprint","IMPRINT",FACE,{"disambiguationData":[TD([[makeQuery(id+"F0.imprint","IMPRINT",EDGE,{"derivedFrom":subQ5}),-1.0]])]});}
            var Q164;
            {var subQ0=sQuery(id+"F0.wireOp",EDGE,"cnf2VEEc-4Zg4-0GWT-UI53-5JaVadr4v9Of.top");var subQ1=sQuery(id+"F0.wireOp",EDGE,"57e6ceb0-2b07-4070-b827-d5ddd958e3c5");var subQ2=makeQuery(id+"F0.imprint","INTERSECT",VERTEX,{"derivedFrom":[subQ1,subQ0]});Q164=makeQuery(id+"F0.imprint","IMPRINT",FACE,{"disambiguationData":[TD([[makeQuery(id+"F0.imprint","IMPRINT",EDGE,{"disambiguationData":[TD([[subQ2,-1.0]])],"derivedFrom":subQ1}),1.0]])]});}
            var Q165;
            {var subQ0=sQuery(id+"F0.wireOp",EDGE,"cnf2VEEc-4Zg4-0GWT-UI53-5JaVadr4v9Of.top");var subQ1=sQuery(id+"F0.wireOp",EDGE,"57e6ceb0-2b07-4070-b827-d5ddd958e3c5");var subQ2=makeQuery(id+"F0.imprint","INTERSECT",VERTEX,{"derivedFrom":[subQ1,subQ0]});Q165=makeQuery(id+"F0.imprint","IMPRINT",FACE,{"disambiguationData":[TD([[makeQuery(id+"F0.imprint","IMPRINT",EDGE,{"disambiguationData":[TD([[subQ2,-1.0]])],"derivedFrom":subQ1}),-1.0]])]});}
            var Q166;
            {var subQ6=sQuery(id+"F0.wireOp",EDGE,"b4aa0741-1242-410c-92f0-afa46b6d95e5.right");Q166=makeQuery(id+"F0.imprint","IMPRINT",FACE,{"disambiguationData":[TD([[makeQuery(id+"F0.imprint","IMPRINT",EDGE,{"derivedFrom":subQ6}),-1.0]])]});}
            var Q167;
            {var subQ1=sQuery(id+"F0.wireOp",EDGE,"b4aa0741-1242-410c-92f0-afa46b6d95e5.left");Q167=makeQuery(id+"F0.imprint","IMPRINT",FACE,{"disambiguationData":[TD([[makeQuery(id+"F0.imprint","IMPRINT",EDGE,{"derivedFrom":subQ1}),1.0]])]});}
            var Q168;
            {var subQ1=sQuery(id+"F0.wireOp",EDGE,"E114.right");Q168=makeQuery(id+"F0.imprint","IMPRINT",FACE,{"disambiguationData":[TD([[makeQuery(id+"F0.imprint","IMPRINT",EDGE,{"derivedFrom":subQ1}),-1.0]])]});}
            var Q169;
            Q169=makeQuery(id+"F0.imprint","IMPRINT",FACE,{"disambiguationData":[TD([[makeQuery(id+"F0.imprint","IMPRINT",EDGE,{"derivedFrom":sQuery(id+"F0.wireOp",EDGE,"E0.right")}),-1.0]])]});
            var Q170;
            {var subQ0=sQuery(id+"F0.wireOp",EDGE,"E123.bottom");Q170=makeQuery(id+"F0.imprint","IMPRINT",FACE,{"disambiguationData":[TD([[makeQuery(id+"F0.imprint","IMPRINT",EDGE,{"derivedFrom":subQ0}),1.0]])]});}
            extrude(context, id + "F1", {"entities" : qUnion([Q0, Q1, Q2, Q3, Q4, Q5, Q6, Q7, Q8, Q9, Q10, Q11, Q12, Q13, Q14, Q15, Q16, Q17, Q18, Q19, Q20, Q21, Q22, Q23, Q24, Q25, Q26, Q27, Q28, Q29, Q30, Q31, Q32, Q33, Q34, Q35, Q36, Q37, Q38, Q39, Q40, Q41, Q42, Q43, Q44, Q45, Q46, Q47, Q48, Q49, Q50, Q51, Q52, Q53, Q54, Q55, Q56, Q57, Q58, Q59, Q60, Q61, Q62, Q63, Q64, Q65, Q66, Q67, Q68, Q69, Q70, Q71, Q72, Q73, Q74, Q75, Q76, Q77, Q78, Q79, Q80, Q81, Q82, Q83, Q84, Q85, Q86, Q87, Q88, Q89, Q90, Q91, Q92, Q93, Q94, Q95, Q96, Q97, Q98, Q99, Q100, Q101, Q102, Q103, Q104, Q105, Q106, Q107, Q108, Q109, Q110, Q111, Q112, Q113, Q114, Q115, Q116, Q117, Q118, Q119, Q120, Q121, Q122, Q123, Q124, Q125, Q126, Q127, Q128, Q129, Q130, Q131, Q132, Q133, Q134, Q135, Q136, Q137, Q138, Q139, Q140, Q141, Q142, Q143, Q144, Q145, Q146, Q147, Q148, Q149, Q150, Q151, Q152, Q153, Q154, Q155, Q156, Q157, Q158, Q159, Q160, Q161, Q162, Q163, Q164, Q165, Q166, Q167, Q168, Q169, Q170]), "depth" : 6.35 * mm});
        }
    });
